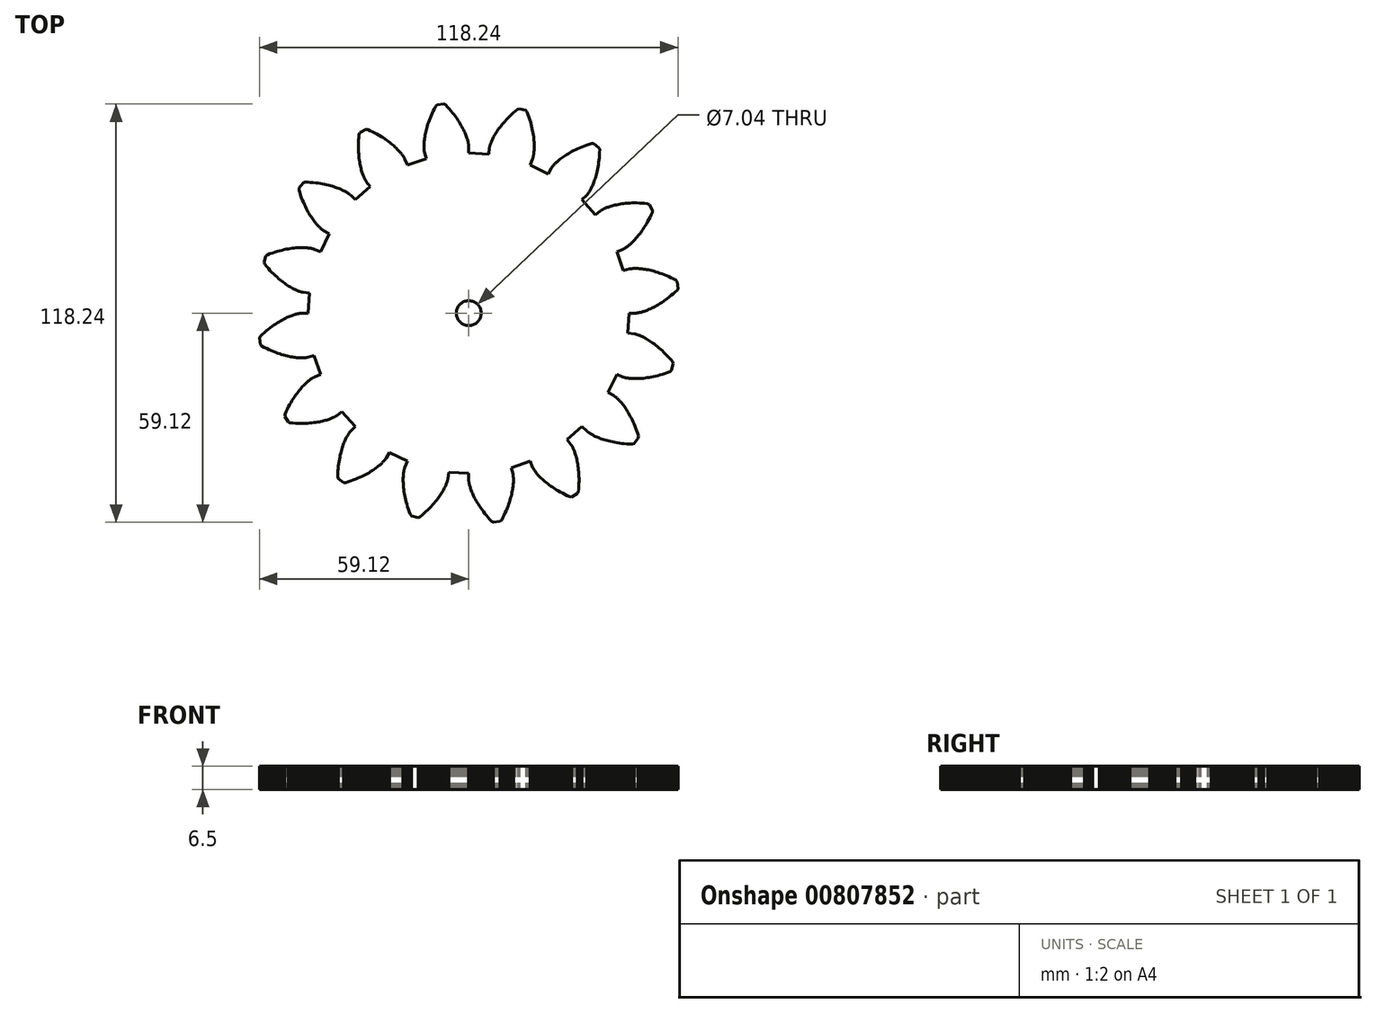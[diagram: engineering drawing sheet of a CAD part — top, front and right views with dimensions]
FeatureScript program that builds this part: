
annotation { "Feature Type Name" : "Feature", "Feature Type Description" : "" }
export const myFeature = defineFeature(function(context is Context, id is Id, definition is map)
    precondition{}
    {
        {
            var Q0;
            Q0=qCreatedBy(makeId("Top.planeOp"),FACE);
            var sketch = newSketch(context, id + "F0", { "sketchPlane" : qUnion([Q0])});
            skLineSegment(sketch, "E0", {"start": v(45.31, 0) * mm, "end": v(47.16, 0) * mm});
            skLineSegment(sketch, "E1", {"start": v(47.16, 0) * mm, "end": v(47.19, 0) * mm});
            skLineSegment(sketch, "E2", {"start": v(47.19, 0) * mm, "end": v(47.24, 0) * mm});
            skLineSegment(sketch, "E3", {"start": v(47.24, 0) * mm, "end": v(47.31, 0) * mm});
            skLineSegment(sketch, "E4", {"start": v(47.31, 0) * mm, "end": v(47.4, 0.02) * mm});
            skLineSegment(sketch, "E5", {"start": v(47.4, 0.02) * mm, "end": v(47.52, 0.03) * mm});
            skLineSegment(sketch, "E6", {"start": v(47.52, 0.03) * mm, "end": v(47.66, 0.05) * mm});
            skLineSegment(sketch, "E7", {"start": v(47.66, 0.05) * mm, "end": v(47.83, 0.08) * mm});
            skLineSegment(sketch, "E8", {"start": v(47.83, 0.08) * mm, "end": v(48, 0.11) * mm});
            skLineSegment(sketch, "E9", {"start": v(48, 0.11) * mm, "end": v(48.21, 0.15) * mm});
            skLineSegment(sketch, "E10", {"start": v(48.21, 0.15) * mm, "end": v(48.44, 0.2) * mm});
            skLineSegment(sketch, "E11", {"start": v(48.44, 0.2) * mm, "end": v(48.69, 0.27) * mm});
            skLineSegment(sketch, "E12", {"start": v(48.69, 0.27) * mm, "end": v(48.95, 0.34) * mm});
            skLineSegment(sketch, "E13", {"start": v(48.95, 0.34) * mm, "end": v(49.24, 0.42) * mm});
            skLineSegment(sketch, "E14", {"start": v(49.24, 0.42) * mm, "end": v(49.54, 0.52) * mm});
            skLineSegment(sketch, "E15", {"start": v(49.54, 0.52) * mm, "end": v(49.87, 0.64) * mm});
            skLineSegment(sketch, "E16", {"start": v(49.87, 0.64) * mm, "end": v(50.21, 0.76) * mm});
            skLineSegment(sketch, "E17", {"start": v(50.21, 0.76) * mm, "end": v(50.57, 0.9) * mm});
            skLineSegment(sketch, "E18", {"start": v(50.57, 0.9) * mm, "end": v(50.95, 1.07) * mm});
            skLineSegment(sketch, "E19", {"start": v(50.95, 1.07) * mm, "end": v(51.34, 1.24) * mm});
            skLineSegment(sketch, "E20", {"start": v(51.34, 1.24) * mm, "end": v(51.76, 1.44) * mm});
            skLineSegment(sketch, "E21", {"start": v(51.76, 1.44) * mm, "end": v(52.18, 1.65) * mm});
            skLineSegment(sketch, "E22", {"start": v(52.18, 1.65) * mm, "end": v(52.63, 1.89) * mm});
            skLineSegment(sketch, "E23", {"start": v(52.63, 1.89) * mm, "end": v(53.08, 2.14) * mm});
            skLineSegment(sketch, "E24", {"start": v(53.08, 2.14) * mm, "end": v(53.55, 2.42) * mm});
            skLineSegment(sketch, "E25", {"start": v(53.55, 2.42) * mm, "end": v(54.04, 2.71) * mm});
            skLineSegment(sketch, "E26", {"start": v(54.04, 2.71) * mm, "end": v(54.53, 3.04) * mm});
            skLineSegment(sketch, "E27", {"start": v(54.53, 3.04) * mm, "end": v(55.04, 3.38) * mm});
            skLineSegment(sketch, "E28", {"start": v(55.04, 3.38) * mm, "end": v(55.56, 3.75) * mm});
            skLineSegment(sketch, "E29", {"start": v(55.56, 3.75) * mm, "end": v(56.08, 4.14) * mm});
            skLineSegment(sketch, "E30", {"start": v(56.08, 4.14) * mm, "end": v(56.62, 4.56) * mm});
            skLineSegment(sketch, "E31", {"start": v(56.62, 4.56) * mm, "end": v(57.17, 5) * mm});
            skLineSegment(sketch, "E32", {"start": v(57.17, 5) * mm, "end": v(57.72, 5.47) * mm});
            skLineSegment(sketch, "E33", {"start": v(57.72, 5.47) * mm, "end": v(58.28, 5.97) * mm});
            skLineSegment(sketch, "E34", {"start": v(58.28, 5.97) * mm, "end": v(58.84, 6.49) * mm});
            skLineSegment(sketch, "E35", {"start": v(58.84, 6.49) * mm, "end": v(59.12, 7) * mm});
            skLineSegment(sketch, "E36", {"start": v(59.12, 7) * mm, "end": v(58.86, 8.9) * mm});
            skLineSegment(sketch, "E37", {"start": v(58.86, 8.9) * mm, "end": v(58.46, 9.33) * mm});
            skLineSegment(sketch, "E38", {"start": v(58.46, 9.33) * mm, "end": v(57.78, 9.68) * mm});
            skLineSegment(sketch, "E39", {"start": v(57.78, 9.68) * mm, "end": v(57.1, 10.01) * mm});
            skLineSegment(sketch, "E40", {"start": v(57.1, 10.01) * mm, "end": v(56.45, 10.32) * mm});
            skLineSegment(sketch, "E41", {"start": v(56.45, 10.32) * mm, "end": v(55.8, 10.6) * mm});
            skLineSegment(sketch, "E42", {"start": v(55.8, 10.6) * mm, "end": v(55.18, 10.86) * mm});
            skLineSegment(sketch, "E43", {"start": v(55.18, 10.86) * mm, "end": v(54.57, 11.1) * mm});
            skLineSegment(sketch, "E44", {"start": v(54.57, 11.1) * mm, "end": v(53.97, 11.32) * mm});
            skLineSegment(sketch, "E45", {"start": v(53.97, 11.32) * mm, "end": v(53.39, 11.52) * mm});
            skLineSegment(sketch, "E46", {"start": v(53.39, 11.52) * mm, "end": v(52.83, 11.7) * mm});
            skLineSegment(sketch, "E47", {"start": v(52.83, 11.7) * mm, "end": v(52.28, 11.85) * mm});
            skLineSegment(sketch, "E48", {"start": v(52.28, 11.85) * mm, "end": v(51.76, 12) * mm});
            skLineSegment(sketch, "E49", {"start": v(51.76, 12) * mm, "end": v(51.25, 12.12) * mm});
            skLineSegment(sketch, "E50", {"start": v(51.25, 12.12) * mm, "end": v(50.76, 12.23) * mm});
            skLineSegment(sketch, "E51", {"start": v(50.76, 12.23) * mm, "end": v(50.3, 12.32) * mm});
            skLineSegment(sketch, "E52", {"start": v(50.3, 12.32) * mm, "end": v(49.84, 12.4) * mm});
            skLineSegment(sketch, "E53", {"start": v(49.84, 12.4) * mm, "end": v(49.41, 12.46) * mm});
            skLineSegment(sketch, "E54", {"start": v(49.41, 12.46) * mm, "end": v(49, 12.52) * mm});
            skLineSegment(sketch, "E55", {"start": v(49, 12.52) * mm, "end": v(48.62, 12.56) * mm});
            skLineSegment(sketch, "E56", {"start": v(48.62, 12.56) * mm, "end": v(48.26, 12.6) * mm});
            skLineSegment(sketch, "E57", {"start": v(48.26, 12.6) * mm, "end": v(47.91, 12.62) * mm});
            skLineSegment(sketch, "E58", {"start": v(47.91, 12.62) * mm, "end": v(47.6, 12.63) * mm});
            skLineSegment(sketch, "E59", {"start": v(47.6, 12.63) * mm, "end": v(47.3, 12.64) * mm});
            skLineSegment(sketch, "E60", {"start": v(47.3, 12.64) * mm, "end": v(47.02, 12.64) * mm});
            skLineSegment(sketch, "E61", {"start": v(47.02, 12.64) * mm, "end": v(46.76, 12.63) * mm});
            skLineSegment(sketch, "E62", {"start": v(46.76, 12.63) * mm, "end": v(46.53, 12.62) * mm});
            skLineSegment(sketch, "E63", {"start": v(46.53, 12.62) * mm, "end": v(46.33, 12.6) * mm});
            skLineSegment(sketch, "E64", {"start": v(46.33, 12.6) * mm, "end": v(46.14, 12.6) * mm});
            skLineSegment(sketch, "E65", {"start": v(46.14, 12.6) * mm, "end": v(45.98, 12.57) * mm});
            skLineSegment(sketch, "E66", {"start": v(45.98, 12.57) * mm, "end": v(45.84, 12.56) * mm});
            skLineSegment(sketch, "E67", {"start": v(45.84, 12.56) * mm, "end": v(45.72, 12.54) * mm});
            skLineSegment(sketch, "E68", {"start": v(45.72, 12.54) * mm, "end": v(45.62, 12.52) * mm});
            skLineSegment(sketch, "E69", {"start": v(45.62, 12.52) * mm, "end": v(45.55, 12.5) * mm});
            skLineSegment(sketch, "E70", {"start": v(45.55, 12.5) * mm, "end": v(45.5, 12.5) * mm});
            skLineSegment(sketch, "E71", {"start": v(45.5, 12.5) * mm, "end": v(45.47, 12.49) * mm});
            skLineSegment(sketch, "E72", {"start": v(45.47, 12.49) * mm, "end": v(43.7, 12) * mm});
            skLineSegment(sketch, "E73", {"start": v(43.7, 12) * mm, "end": v(41.86, 17.34) * mm});
            skLineSegment(sketch, "E74", {"start": v(41.86, 17.34) * mm, "end": v(43.57, 18.05) * mm});
            skLineSegment(sketch, "E75", {"start": v(43.57, 18.05) * mm, "end": v(43.6, 18.06) * mm});
            skLineSegment(sketch, "E76", {"start": v(43.6, 18.06) * mm, "end": v(43.64, 18.08) * mm});
            skLineSegment(sketch, "E77", {"start": v(43.64, 18.08) * mm, "end": v(43.7, 18.11) * mm});
            skLineSegment(sketch, "E78", {"start": v(43.7, 18.11) * mm, "end": v(43.8, 18.16) * mm});
            skLineSegment(sketch, "E79", {"start": v(43.8, 18.16) * mm, "end": v(43.9, 18.22) * mm});
            skLineSegment(sketch, "E80", {"start": v(43.9, 18.22) * mm, "end": v(44.02, 18.29) * mm});
            skLineSegment(sketch, "E81", {"start": v(44.02, 18.29) * mm, "end": v(44.16, 18.37) * mm});
            skLineSegment(sketch, "E82", {"start": v(44.16, 18.37) * mm, "end": v(44.31, 18.48) * mm});
            skLineSegment(sketch, "E83", {"start": v(44.31, 18.48) * mm, "end": v(44.49, 18.6) * mm});
            skLineSegment(sketch, "E84", {"start": v(44.49, 18.6) * mm, "end": v(44.67, 18.73) * mm});
            skLineSegment(sketch, "E85", {"start": v(44.67, 18.73) * mm, "end": v(44.88, 18.88) * mm});
            skLineSegment(sketch, "E86", {"start": v(44.88, 18.88) * mm, "end": v(45.1, 19.05) * mm});
            skLineSegment(sketch, "E87", {"start": v(45.1, 19.05) * mm, "end": v(45.33, 19.23) * mm});
            skLineSegment(sketch, "E88", {"start": v(45.33, 19.23) * mm, "end": v(45.57, 19.44) * mm});
            skLineSegment(sketch, "E89", {"start": v(45.57, 19.44) * mm, "end": v(45.83, 19.67) * mm});
            skLineSegment(sketch, "E90", {"start": v(45.83, 19.67) * mm, "end": v(46.1, 19.92) * mm});
            skLineSegment(sketch, "E91", {"start": v(46.1, 19.92) * mm, "end": v(46.38, 20.2) * mm});
            skLineSegment(sketch, "E92", {"start": v(46.38, 20.2) * mm, "end": v(46.66, 20.48) * mm});
            skLineSegment(sketch, "E93", {"start": v(46.66, 20.48) * mm, "end": v(46.96, 20.8) * mm});
            skLineSegment(sketch, "E94", {"start": v(46.96, 20.8) * mm, "end": v(47.27, 21.13) * mm});
            skLineSegment(sketch, "E95", {"start": v(47.27, 21.13) * mm, "end": v(47.58, 21.5) * mm});
            skLineSegment(sketch, "E96", {"start": v(47.58, 21.5) * mm, "end": v(47.9, 21.88) * mm});
            skLineSegment(sketch, "E97", {"start": v(47.9, 21.88) * mm, "end": v(48.22, 22.3) * mm});
            skLineSegment(sketch, "E98", {"start": v(48.22, 22.3) * mm, "end": v(48.55, 22.73) * mm});
            skLineSegment(sketch, "E99", {"start": v(48.55, 22.73) * mm, "end": v(48.88, 23.19) * mm});
            skLineSegment(sketch, "E100", {"start": v(48.88, 23.19) * mm, "end": v(49.22, 23.67) * mm});
            skLineSegment(sketch, "E101", {"start": v(49.22, 23.67) * mm, "end": v(49.56, 24.18) * mm});
            skLineSegment(sketch, "E102", {"start": v(49.56, 24.18) * mm, "end": v(49.9, 24.72) * mm});
            skLineSegment(sketch, "E103", {"start": v(49.9, 24.72) * mm, "end": v(50.23, 25.29) * mm});
            skLineSegment(sketch, "E104", {"start": v(50.23, 25.29) * mm, "end": v(50.57, 25.88) * mm});
            skLineSegment(sketch, "E105", {"start": v(50.57, 25.88) * mm, "end": v(50.9, 26.5) * mm});
            skLineSegment(sketch, "E106", {"start": v(50.9, 26.5) * mm, "end": v(51.23, 27.14) * mm});
            skLineSegment(sketch, "E107", {"start": v(51.23, 27.14) * mm, "end": v(51.56, 27.81) * mm});
            skLineSegment(sketch, "E108", {"start": v(51.56, 27.81) * mm, "end": v(51.88, 28.51) * mm});
            skLineSegment(sketch, "E109", {"start": v(51.88, 28.51) * mm, "end": v(51.94, 29.1) * mm});
            skLineSegment(sketch, "E110", {"start": v(51.94, 29.1) * mm, "end": v(50.98, 30.75) * mm});
            skLineSegment(sketch, "E111", {"start": v(50.98, 30.75) * mm, "end": v(50.44, 30.99) * mm});
            skLineSegment(sketch, "E112", {"start": v(50.44, 30.99) * mm, "end": v(49.67, 31.05) * mm});
            skLineSegment(sketch, "E113", {"start": v(49.67, 31.05) * mm, "end": v(48.93, 31.1) * mm});
            skLineSegment(sketch, "E114", {"start": v(48.93, 31.1) * mm, "end": v(48.2, 31.14) * mm});
            skLineSegment(sketch, "E115", {"start": v(48.2, 31.14) * mm, "end": v(47.5, 31.15) * mm});
            skLineSegment(sketch, "E116", {"start": v(47.5, 31.15) * mm, "end": v(46.82, 31.15) * mm});
            skLineSegment(sketch, "E117", {"start": v(46.82, 31.15) * mm, "end": v(46.16, 31.14) * mm});
            skLineSegment(sketch, "E118", {"start": v(46.16, 31.14) * mm, "end": v(45.53, 31.1) * mm});
            skLineSegment(sketch, "E119", {"start": v(45.53, 31.1) * mm, "end": v(44.92, 31.07) * mm});
            skLineSegment(sketch, "E120", {"start": v(44.92, 31.07) * mm, "end": v(44.33, 31.02) * mm});
            skLineSegment(sketch, "E121", {"start": v(44.33, 31.02) * mm, "end": v(43.77, 30.96) * mm});
            skLineSegment(sketch, "E122", {"start": v(43.77, 30.96) * mm, "end": v(43.23, 30.89) * mm});
            skLineSegment(sketch, "E123", {"start": v(43.23, 30.89) * mm, "end": v(42.7, 30.8) * mm});
            skLineSegment(sketch, "E124", {"start": v(42.7, 30.8) * mm, "end": v(42.22, 30.72) * mm});
            skLineSegment(sketch, "E125", {"start": v(42.22, 30.72) * mm, "end": v(41.75, 30.63) * mm});
            skLineSegment(sketch, "E126", {"start": v(41.75, 30.63) * mm, "end": v(41.3, 30.53) * mm});
            skLineSegment(sketch, "E127", {"start": v(41.3, 30.53) * mm, "end": v(40.88, 30.43) * mm});
            skLineSegment(sketch, "E128", {"start": v(40.88, 30.43) * mm, "end": v(40.49, 30.32) * mm});
            skLineSegment(sketch, "E129", {"start": v(40.49, 30.32) * mm, "end": v(40.11, 30.21) * mm});
            skLineSegment(sketch, "E130", {"start": v(40.11, 30.21) * mm, "end": v(39.76, 30.1) * mm});
            skLineSegment(sketch, "E131", {"start": v(39.76, 30.1) * mm, "end": v(39.44, 30) * mm});
            skLineSegment(sketch, "E132", {"start": v(39.44, 30) * mm, "end": v(39.14, 29.88) * mm});
            skLineSegment(sketch, "E133", {"start": v(39.14, 29.88) * mm, "end": v(38.86, 29.77) * mm});
            skLineSegment(sketch, "E134", {"start": v(38.86, 29.77) * mm, "end": v(38.6, 29.67) * mm});
            skLineSegment(sketch, "E135", {"start": v(38.6, 29.67) * mm, "end": v(38.37, 29.57) * mm});
            skLineSegment(sketch, "E136", {"start": v(38.37, 29.57) * mm, "end": v(38.16, 29.47) * mm});
            skLineSegment(sketch, "E137", {"start": v(38.16, 29.47) * mm, "end": v(37.97, 29.38) * mm});
            skLineSegment(sketch, "E138", {"start": v(37.97, 29.38) * mm, "end": v(37.8, 29.3) * mm});
            skLineSegment(sketch, "E139", {"start": v(37.8, 29.3) * mm, "end": v(37.67, 29.21) * mm});
            skLineSegment(sketch, "E140", {"start": v(37.67, 29.21) * mm, "end": v(37.54, 29.14) * mm});
            skLineSegment(sketch, "E141", {"start": v(37.54, 29.14) * mm, "end": v(37.44, 29.08) * mm});
            skLineSegment(sketch, "E142", {"start": v(37.44, 29.08) * mm, "end": v(37.36, 29.03) * mm});
            skLineSegment(sketch, "E143", {"start": v(37.36, 29.03) * mm, "end": v(37.3, 28.99) * mm});
            skLineSegment(sketch, "E144", {"start": v(37.3, 28.99) * mm, "end": v(37.26, 28.96) * mm});
            skLineSegment(sketch, "E145", {"start": v(37.26, 28.96) * mm, "end": v(37.23, 28.94) * mm});
            skLineSegment(sketch, "E146", {"start": v(37.23, 28.94) * mm, "end": v(35.77, 27.8) * mm});
            skLineSegment(sketch, "E147", {"start": v(35.77, 27.8) * mm, "end": v(32.04, 32.04) * mm});
            skLineSegment(sketch, "E148", {"start": v(32.04, 32.04) * mm, "end": v(33.34, 33.34) * mm});
            skLineSegment(sketch, "E149", {"start": v(33.34, 33.34) * mm, "end": v(33.36, 33.37) * mm});
            skLineSegment(sketch, "E150", {"start": v(33.36, 33.37) * mm, "end": v(33.4, 33.4) * mm});
            skLineSegment(sketch, "E151", {"start": v(33.4, 33.4) * mm, "end": v(33.45, 33.46) * mm});
            skLineSegment(sketch, "E152", {"start": v(33.45, 33.46) * mm, "end": v(33.5, 33.53) * mm});
            skLineSegment(sketch, "E153", {"start": v(33.5, 33.53) * mm, "end": v(33.58, 33.63) * mm});
            skLineSegment(sketch, "E154", {"start": v(33.58, 33.63) * mm, "end": v(33.67, 33.74) * mm});
            skLineSegment(sketch, "E155", {"start": v(33.67, 33.74) * mm, "end": v(33.76, 33.87) * mm});
            skLineSegment(sketch, "E156", {"start": v(33.76, 33.87) * mm, "end": v(33.87, 34.03) * mm});
            skLineSegment(sketch, "E157", {"start": v(33.87, 34.03) * mm, "end": v(33.99, 34.2) * mm});
            skLineSegment(sketch, "E158", {"start": v(33.99, 34.2) * mm, "end": v(34.1, 34.4) * mm});
            skLineSegment(sketch, "E159", {"start": v(34.1, 34.4) * mm, "end": v(34.24, 34.61) * mm});
            skLineSegment(sketch, "E160", {"start": v(34.24, 34.61) * mm, "end": v(34.37, 34.85) * mm});
            skLineSegment(sketch, "E161", {"start": v(34.37, 34.85) * mm, "end": v(34.52, 35.12) * mm});
            skLineSegment(sketch, "E162", {"start": v(34.52, 35.12) * mm, "end": v(34.66, 35.4) * mm});
            skLineSegment(sketch, "E163", {"start": v(34.66, 35.4) * mm, "end": v(34.81, 35.71) * mm});
            skLineSegment(sketch, "E164", {"start": v(34.81, 35.71) * mm, "end": v(34.96, 36.04) * mm});
            skLineSegment(sketch, "E165", {"start": v(34.96, 36.04) * mm, "end": v(35.12, 36.4) * mm});
            skLineSegment(sketch, "E166", {"start": v(35.12, 36.4) * mm, "end": v(35.27, 36.78) * mm});
            skLineSegment(sketch, "E167", {"start": v(35.27, 36.78) * mm, "end": v(35.43, 37.18) * mm});
            skLineSegment(sketch, "E168", {"start": v(35.43, 37.18) * mm, "end": v(35.58, 37.61) * mm});
            skLineSegment(sketch, "E169", {"start": v(35.58, 37.61) * mm, "end": v(35.73, 38.07) * mm});
            skLineSegment(sketch, "E170", {"start": v(35.73, 38.07) * mm, "end": v(35.88, 38.55) * mm});
            skLineSegment(sketch, "E171", {"start": v(35.88, 38.55) * mm, "end": v(36.02, 39.05) * mm});
            skLineSegment(sketch, "E172", {"start": v(36.02, 39.05) * mm, "end": v(36.16, 39.58) * mm});
            skLineSegment(sketch, "E173", {"start": v(36.16, 39.58) * mm, "end": v(36.3, 40.13) * mm});
            skLineSegment(sketch, "E174", {"start": v(36.3, 40.13) * mm, "end": v(36.41, 40.7) * mm});
            skLineSegment(sketch, "E175", {"start": v(36.41, 40.7) * mm, "end": v(36.53, 41.3) * mm});
            skLineSegment(sketch, "E176", {"start": v(36.53, 41.3) * mm, "end": v(36.64, 41.93) * mm});
            skLineSegment(sketch, "E177", {"start": v(36.64, 41.93) * mm, "end": v(36.73, 42.58) * mm});
            skLineSegment(sketch, "E178", {"start": v(36.73, 42.58) * mm, "end": v(36.82, 43.26) * mm});
            skLineSegment(sketch, "E179", {"start": v(36.82, 43.26) * mm, "end": v(36.89, 43.96) * mm});
            skLineSegment(sketch, "E180", {"start": v(36.89, 43.96) * mm, "end": v(36.95, 44.68) * mm});
            skLineSegment(sketch, "E181", {"start": v(36.95, 44.68) * mm, "end": v(36.99, 45.43) * mm});
            skLineSegment(sketch, "E182", {"start": v(36.99, 45.43) * mm, "end": v(37.02, 46.2) * mm});
            skLineSegment(sketch, "E183", {"start": v(37.02, 46.2) * mm, "end": v(36.85, 46.76) * mm});
            skLineSegment(sketch, "E184", {"start": v(36.85, 46.76) * mm, "end": v(35.33, 47.91) * mm});
            skLineSegment(sketch, "E185", {"start": v(35.33, 47.91) * mm, "end": v(34.74, 47.93) * mm});
            skLineSegment(sketch, "E186", {"start": v(34.74, 47.93) * mm, "end": v(34, 47.7) * mm});
            skLineSegment(sketch, "E187", {"start": v(34, 47.7) * mm, "end": v(33.3, 47.46) * mm});
            skLineSegment(sketch, "E188", {"start": v(33.3, 47.46) * mm, "end": v(32.62, 47.21) * mm});
            skLineSegment(sketch, "E189", {"start": v(32.62, 47.21) * mm, "end": v(31.96, 46.96) * mm});
            skLineSegment(sketch, "E190", {"start": v(31.96, 46.96) * mm, "end": v(31.34, 46.7) * mm});
            skLineSegment(sketch, "E191", {"start": v(31.34, 46.7) * mm, "end": v(30.73, 46.43) * mm});
            skLineSegment(sketch, "E192", {"start": v(30.73, 46.43) * mm, "end": v(30.16, 46.16) * mm});
            skLineSegment(sketch, "E193", {"start": v(30.16, 46.16) * mm, "end": v(29.61, 45.9) * mm});
            skLineSegment(sketch, "E194", {"start": v(29.61, 45.9) * mm, "end": v(29.09, 45.62) * mm});
            skLineSegment(sketch, "E195", {"start": v(29.09, 45.62) * mm, "end": v(28.59, 45.35) * mm});
            skLineSegment(sketch, "E196", {"start": v(28.59, 45.35) * mm, "end": v(28.12, 45.08) * mm});
            skLineSegment(sketch, "E197", {"start": v(28.12, 45.08) * mm, "end": v(27.67, 44.8) * mm});
            skLineSegment(sketch, "E198", {"start": v(27.67, 44.8) * mm, "end": v(27.25, 44.54) * mm});
            skLineSegment(sketch, "E199", {"start": v(27.25, 44.54) * mm, "end": v(26.85, 44.27) * mm});
            skLineSegment(sketch, "E200", {"start": v(26.85, 44.27) * mm, "end": v(26.48, 44.01) * mm});
            skLineSegment(sketch, "E201", {"start": v(26.48, 44.01) * mm, "end": v(26.13, 43.75) * mm});
            skLineSegment(sketch, "E202", {"start": v(26.13, 43.75) * mm, "end": v(25.8, 43.5) * mm});
            skLineSegment(sketch, "E203", {"start": v(25.8, 43.5) * mm, "end": v(25.5, 43.26) * mm});
            skLineSegment(sketch, "E204", {"start": v(25.5, 43.26) * mm, "end": v(25.22, 43.03) * mm});
            skLineSegment(sketch, "E205", {"start": v(25.22, 43.03) * mm, "end": v(24.96, 42.8) * mm});
            skLineSegment(sketch, "E206", {"start": v(24.96, 42.8) * mm, "end": v(24.72, 42.58) * mm});
            skLineSegment(sketch, "E207", {"start": v(24.72, 42.58) * mm, "end": v(24.5, 42.38) * mm});
            skLineSegment(sketch, "E208", {"start": v(24.5, 42.38) * mm, "end": v(24.31, 42.18) * mm});
            skLineSegment(sketch, "E209", {"start": v(24.31, 42.18) * mm, "end": v(24.14, 42) * mm});
            skLineSegment(sketch, "E210", {"start": v(24.14, 42) * mm, "end": v(23.98, 41.83) * mm});
            skLineSegment(sketch, "E211", {"start": v(23.98, 41.83) * mm, "end": v(23.84, 41.67) * mm});
            skLineSegment(sketch, "E212", {"start": v(23.84, 41.67) * mm, "end": v(23.72, 41.53) * mm});
            skLineSegment(sketch, "E213", {"start": v(23.72, 41.53) * mm, "end": v(23.62, 41.4) * mm});
            skLineSegment(sketch, "E214", {"start": v(23.62, 41.4) * mm, "end": v(23.53, 41.29) * mm});
            skLineSegment(sketch, "E215", {"start": v(23.53, 41.29) * mm, "end": v(23.46, 41.2) * mm});
            skLineSegment(sketch, "E216", {"start": v(23.46, 41.2) * mm, "end": v(23.4, 41.12) * mm});
            skLineSegment(sketch, "E217", {"start": v(23.4, 41.12) * mm, "end": v(23.37, 41.05) * mm});
            skLineSegment(sketch, "E218", {"start": v(23.37, 41.05) * mm, "end": v(23.34, 41) * mm});
            skLineSegment(sketch, "E219", {"start": v(23.34, 41) * mm, "end": v(23.32, 40.98) * mm});
            skLineSegment(sketch, "E220", {"start": v(23.32, 40.98) * mm, "end": v(22.4, 39.38) * mm});
            skLineSegment(sketch, "E221", {"start": v(22.4, 39.38) * mm, "end": v(17.34, 41.86) * mm});
            skLineSegment(sketch, "E222", {"start": v(17.34, 41.86) * mm, "end": v(18.05, 43.57) * mm});
            skLineSegment(sketch, "E223", {"start": v(18.05, 43.57) * mm, "end": v(18.06, 43.6) * mm});
            skLineSegment(sketch, "E224", {"start": v(18.06, 43.6) * mm, "end": v(18.07, 43.64) * mm});
            skLineSegment(sketch, "E225", {"start": v(18.07, 43.64) * mm, "end": v(18.1, 43.71) * mm});
            skLineSegment(sketch, "E226", {"start": v(18.1, 43.71) * mm, "end": v(18.13, 43.8) * mm});
            skLineSegment(sketch, "E227", {"start": v(18.13, 43.8) * mm, "end": v(18.16, 43.92) * mm});
            skLineSegment(sketch, "E228", {"start": v(18.16, 43.92) * mm, "end": v(18.2, 44.06) * mm});
            skLineSegment(sketch, "E229", {"start": v(18.2, 44.06) * mm, "end": v(18.23, 44.22) * mm});
            skLineSegment(sketch, "E230", {"start": v(18.23, 44.22) * mm, "end": v(18.27, 44.4) * mm});
            skLineSegment(sketch, "E231", {"start": v(18.27, 44.4) * mm, "end": v(18.3, 44.6) * mm});
            skLineSegment(sketch, "E232", {"start": v(18.3, 44.6) * mm, "end": v(18.35, 44.83) * mm});
            skLineSegment(sketch, "E233", {"start": v(18.35, 44.83) * mm, "end": v(18.39, 45.08) * mm});
            skLineSegment(sketch, "E234", {"start": v(18.39, 45.08) * mm, "end": v(18.42, 45.36) * mm});
            skLineSegment(sketch, "E235", {"start": v(18.42, 45.36) * mm, "end": v(18.45, 45.65) * mm});
            skLineSegment(sketch, "E236", {"start": v(18.45, 45.65) * mm, "end": v(18.48, 45.97) * mm});
            skLineSegment(sketch, "E237", {"start": v(18.48, 45.97) * mm, "end": v(18.5, 46.31) * mm});
            skLineSegment(sketch, "E238", {"start": v(18.5, 46.31) * mm, "end": v(18.51, 46.68) * mm});
            skLineSegment(sketch, "E239", {"start": v(18.51, 46.68) * mm, "end": v(18.52, 47.07) * mm});
            skLineSegment(sketch, "E240", {"start": v(18.52, 47.07) * mm, "end": v(18.51, 47.48) * mm});
            skLineSegment(sketch, "E241", {"start": v(18.51, 47.48) * mm, "end": v(18.5, 47.91) * mm});
            skLineSegment(sketch, "E242", {"start": v(18.5, 47.91) * mm, "end": v(18.48, 48.37) * mm});
            skLineSegment(sketch, "E243", {"start": v(18.48, 48.37) * mm, "end": v(18.44, 48.84) * mm});
            skLineSegment(sketch, "E244", {"start": v(18.44, 48.84) * mm, "end": v(18.4, 49.34) * mm});
            skLineSegment(sketch, "E245", {"start": v(18.4, 49.34) * mm, "end": v(18.34, 49.86) * mm});
            skLineSegment(sketch, "E246", {"start": v(18.34, 49.86) * mm, "end": v(18.26, 50.4) * mm});
            skLineSegment(sketch, "E247", {"start": v(18.26, 50.4) * mm, "end": v(18.17, 50.96) * mm});
            skLineSegment(sketch, "E248", {"start": v(18.17, 50.96) * mm, "end": v(18.06, 51.54) * mm});
            skLineSegment(sketch, "E249", {"start": v(18.06, 51.54) * mm, "end": v(17.94, 52.14) * mm});
            skLineSegment(sketch, "E250", {"start": v(17.94, 52.14) * mm, "end": v(17.8, 52.76) * mm});
            skLineSegment(sketch, "E251", {"start": v(17.8, 52.76) * mm, "end": v(17.64, 53.4) * mm});
            skLineSegment(sketch, "E252", {"start": v(17.64, 53.4) * mm, "end": v(17.46, 54.06) * mm});
            skLineSegment(sketch, "E253", {"start": v(17.46, 54.06) * mm, "end": v(17.26, 54.73) * mm});
            skLineSegment(sketch, "E254", {"start": v(17.26, 54.73) * mm, "end": v(17.04, 55.42) * mm});
            skLineSegment(sketch, "E255", {"start": v(17.04, 55.42) * mm, "end": v(16.8, 56.12) * mm});
            skLineSegment(sketch, "E256", {"start": v(16.8, 56.12) * mm, "end": v(16.52, 56.85) * mm});
            skLineSegment(sketch, "E257", {"start": v(16.52, 56.85) * mm, "end": v(16.15, 57.3) * mm});
            skLineSegment(sketch, "E258", {"start": v(16.15, 57.3) * mm, "end": v(14.3, 57.79) * mm});
            skLineSegment(sketch, "E259", {"start": v(14.3, 57.79) * mm, "end": v(13.76, 57.58) * mm});
            skLineSegment(sketch, "E260", {"start": v(13.76, 57.58) * mm, "end": v(13.17, 57.08) * mm});
            skLineSegment(sketch, "E261", {"start": v(13.17, 57.08) * mm, "end": v(12.6, 56.6) * mm});
            skLineSegment(sketch, "E262", {"start": v(12.6, 56.6) * mm, "end": v(12.07, 56.1) * mm});
            skLineSegment(sketch, "E263", {"start": v(12.07, 56.1) * mm, "end": v(11.56, 55.62) * mm});
            skLineSegment(sketch, "E264", {"start": v(11.56, 55.62) * mm, "end": v(11.08, 55.14) * mm});
            skLineSegment(sketch, "E265", {"start": v(11.08, 55.14) * mm, "end": v(10.63, 54.66) * mm});
            skLineSegment(sketch, "E266", {"start": v(10.63, 54.66) * mm, "end": v(10.2, 54.2) * mm});
            skLineSegment(sketch, "E267", {"start": v(10.2, 54.2) * mm, "end": v(9.8, 53.73) * mm});
            skLineSegment(sketch, "E268", {"start": v(9.8, 53.73) * mm, "end": v(9.41, 53.28) * mm});
            skLineSegment(sketch, "E269", {"start": v(9.41, 53.28) * mm, "end": v(9.06, 52.84) * mm});
            skLineSegment(sketch, "E270", {"start": v(9.06, 52.84) * mm, "end": v(8.73, 52.4) * mm});
            skLineSegment(sketch, "E271", {"start": v(8.73, 52.4) * mm, "end": v(8.42, 51.98) * mm});
            skLineSegment(sketch, "E272", {"start": v(8.42, 51.98) * mm, "end": v(8.13, 51.57) * mm});
            skLineSegment(sketch, "E273", {"start": v(8.13, 51.57) * mm, "end": v(7.86, 51.18) * mm});
            skLineSegment(sketch, "E274", {"start": v(7.86, 51.18) * mm, "end": v(7.62, 50.8) * mm});
            skLineSegment(sketch, "E275", {"start": v(7.62, 50.8) * mm, "end": v(7.4, 50.42) * mm});
            skLineSegment(sketch, "E276", {"start": v(7.4, 50.42) * mm, "end": v(7.19, 50.07) * mm});
            skLineSegment(sketch, "E277", {"start": v(7.19, 50.07) * mm, "end": v(7, 49.73) * mm});
            skLineSegment(sketch, "E278", {"start": v(7, 49.73) * mm, "end": v(6.83, 49.4) * mm});
            skLineSegment(sketch, "E279", {"start": v(6.83, 49.4) * mm, "end": v(6.68, 49.1) * mm});
            skLineSegment(sketch, "E280", {"start": v(6.68, 49.1) * mm, "end": v(6.54, 48.8) * mm});
            skLineSegment(sketch, "E281", {"start": v(6.54, 48.8) * mm, "end": v(6.42, 48.53) * mm});
            skLineSegment(sketch, "E282", {"start": v(6.42, 48.53) * mm, "end": v(6.32, 48.27) * mm});
            skLineSegment(sketch, "E283", {"start": v(6.32, 48.27) * mm, "end": v(6.23, 48.04) * mm});
            skLineSegment(sketch, "E284", {"start": v(6.23, 48.04) * mm, "end": v(6.15, 47.82) * mm});
            skLineSegment(sketch, "E285", {"start": v(6.15, 47.82) * mm, "end": v(6.08, 47.62) * mm});
            skLineSegment(sketch, "E286", {"start": v(6.08, 47.62) * mm, "end": v(6.02, 47.45) * mm});
            skLineSegment(sketch, "E287", {"start": v(6.02, 47.45) * mm, "end": v(5.98, 47.29) * mm});
            skLineSegment(sketch, "E288", {"start": v(5.98, 47.29) * mm, "end": v(5.94, 47.15) * mm});
            skLineSegment(sketch, "E289", {"start": v(5.94, 47.15) * mm, "end": v(5.91, 47.04) * mm});
            skLineSegment(sketch, "E290", {"start": v(5.91, 47.04) * mm, "end": v(5.9, 46.94) * mm});
            skLineSegment(sketch, "E291", {"start": v(5.9, 46.94) * mm, "end": v(5.88, 46.87) * mm});
            skLineSegment(sketch, "E292", {"start": v(5.88, 46.87) * mm, "end": v(5.87, 46.82) * mm});
            skLineSegment(sketch, "E293", {"start": v(5.87, 46.82) * mm, "end": v(5.86, 46.79) * mm});
            skLineSegment(sketch, "E294", {"start": v(5.86, 46.79) * mm, "end": v(5.64, 44.96) * mm});
            skLineSegment(sketch, "E295", {"start": v(5.64, 44.96) * mm, "end": v(0, 45.31) * mm});
            skLineSegment(sketch, "E296", {"start": v(0, 45.31) * mm, "end": v(0, 47.16) * mm});
            skLineSegment(sketch, "E297", {"start": v(0, 47.16) * mm, "end": v(0, 47.19) * mm});
            skLineSegment(sketch, "E298", {"start": v(0, 47.19) * mm, "end": v(0, 47.24) * mm});
            skLineSegment(sketch, "E299", {"start": v(0, 47.24) * mm, "end": v(0, 47.31) * mm});
            skLineSegment(sketch, "E300", {"start": v(0, 47.31) * mm, "end": v(-0.02, 47.4) * mm});
            skLineSegment(sketch, "E301", {"start": v(-0.02, 47.4) * mm, "end": v(-0.03, 47.52) * mm});
            skLineSegment(sketch, "E302", {"start": v(-0.03, 47.52) * mm, "end": v(-0.05, 47.66) * mm});
            skLineSegment(sketch, "E303", {"start": v(-0.05, 47.66) * mm, "end": v(-0.08, 47.83) * mm});
            skLineSegment(sketch, "E304", {"start": v(-0.08, 47.83) * mm, "end": v(-0.1, 48) * mm});
            skLineSegment(sketch, "E305", {"start": v(-0.1, 48) * mm, "end": v(-0.15, 48.21) * mm});
            skLineSegment(sketch, "E306", {"start": v(-0.15, 48.21) * mm, "end": v(-0.2, 48.44) * mm});
            skLineSegment(sketch, "E307", {"start": v(-0.2, 48.44) * mm, "end": v(-0.27, 48.69) * mm});
            skLineSegment(sketch, "E308", {"start": v(-0.27, 48.69) * mm, "end": v(-0.34, 48.95) * mm});
            skLineSegment(sketch, "E309", {"start": v(-0.34, 48.95) * mm, "end": v(-0.42, 49.24) * mm});
            skLineSegment(sketch, "E310", {"start": v(-0.42, 49.24) * mm, "end": v(-0.52, 49.54) * mm});
            skLineSegment(sketch, "E311", {"start": v(-0.52, 49.54) * mm, "end": v(-0.64, 49.87) * mm});
            skLineSegment(sketch, "E312", {"start": v(-0.64, 49.87) * mm, "end": v(-0.76, 50.21) * mm});
            skLineSegment(sketch, "E313", {"start": v(-0.76, 50.21) * mm, "end": v(-0.9, 50.57) * mm});
            skLineSegment(sketch, "E314", {"start": v(-0.9, 50.57) * mm, "end": v(-1.07, 50.95) * mm});
            skLineSegment(sketch, "E315", {"start": v(-1.07, 50.95) * mm, "end": v(-1.24, 51.34) * mm});
            skLineSegment(sketch, "E316", {"start": v(-1.24, 51.34) * mm, "end": v(-1.44, 51.76) * mm});
            skLineSegment(sketch, "E317", {"start": v(-1.44, 51.76) * mm, "end": v(-1.65, 52.18) * mm});
            skLineSegment(sketch, "E318", {"start": v(-1.65, 52.18) * mm, "end": v(-1.89, 52.63) * mm});
            skLineSegment(sketch, "E319", {"start": v(-1.89, 52.63) * mm, "end": v(-2.14, 53.08) * mm});
            skLineSegment(sketch, "E320", {"start": v(-2.14, 53.08) * mm, "end": v(-2.42, 53.55) * mm});
            skLineSegment(sketch, "E321", {"start": v(-2.42, 53.55) * mm, "end": v(-2.71, 54.04) * mm});
            skLineSegment(sketch, "E322", {"start": v(-2.71, 54.04) * mm, "end": v(-3.04, 54.53) * mm});
            skLineSegment(sketch, "E323", {"start": v(-3.04, 54.53) * mm, "end": v(-3.38, 55.04) * mm});
            skLineSegment(sketch, "E324", {"start": v(-3.38, 55.04) * mm, "end": v(-3.75, 55.56) * mm});
            skLineSegment(sketch, "E325", {"start": v(-3.75, 55.56) * mm, "end": v(-4.14, 56.08) * mm});
            skLineSegment(sketch, "E326", {"start": v(-4.14, 56.08) * mm, "end": v(-4.56, 56.62) * mm});
            skLineSegment(sketch, "E327", {"start": v(-4.56, 56.62) * mm, "end": v(-5, 57.17) * mm});
            skLineSegment(sketch, "E328", {"start": v(-5, 57.17) * mm, "end": v(-5.47, 57.72) * mm});
            skLineSegment(sketch, "E329", {"start": v(-5.47, 57.72) * mm, "end": v(-5.97, 58.28) * mm});
            skLineSegment(sketch, "E330", {"start": v(-5.97, 58.28) * mm, "end": v(-6.49, 58.84) * mm});
            skLineSegment(sketch, "E331", {"start": v(-6.49, 58.84) * mm, "end": v(-7, 59.12) * mm});
            skLineSegment(sketch, "E332", {"start": v(-7, 59.12) * mm, "end": v(-8.9, 58.86) * mm});
            skLineSegment(sketch, "E333", {"start": v(-8.9, 58.86) * mm, "end": v(-9.33, 58.46) * mm});
            skLineSegment(sketch, "E334", {"start": v(-9.33, 58.46) * mm, "end": v(-9.68, 57.78) * mm});
            skLineSegment(sketch, "E335", {"start": v(-9.68, 57.78) * mm, "end": v(-10.01, 57.1) * mm});
            skLineSegment(sketch, "E336", {"start": v(-10.01, 57.1) * mm, "end": v(-10.32, 56.45) * mm});
            skLineSegment(sketch, "E337", {"start": v(-10.32, 56.45) * mm, "end": v(-10.6, 55.8) * mm});
            skLineSegment(sketch, "E338", {"start": v(-10.6, 55.8) * mm, "end": v(-10.86, 55.18) * mm});
            skLineSegment(sketch, "E339", {"start": v(-10.86, 55.18) * mm, "end": v(-11.1, 54.57) * mm});
            skLineSegment(sketch, "E340", {"start": v(-11.1, 54.57) * mm, "end": v(-11.32, 53.97) * mm});
            skLineSegment(sketch, "E341", {"start": v(-11.32, 53.97) * mm, "end": v(-11.52, 53.39) * mm});
            skLineSegment(sketch, "E342", {"start": v(-11.52, 53.39) * mm, "end": v(-11.7, 52.83) * mm});
            skLineSegment(sketch, "E343", {"start": v(-11.7, 52.83) * mm, "end": v(-11.85, 52.28) * mm});
            skLineSegment(sketch, "E344", {"start": v(-11.85, 52.28) * mm, "end": v(-12, 51.76) * mm});
            skLineSegment(sketch, "E345", {"start": v(-12, 51.76) * mm, "end": v(-12.12, 51.25) * mm});
            skLineSegment(sketch, "E346", {"start": v(-12.12, 51.25) * mm, "end": v(-12.23, 50.76) * mm});
            skLineSegment(sketch, "E347", {"start": v(-12.23, 50.76) * mm, "end": v(-12.32, 50.3) * mm});
            skLineSegment(sketch, "E348", {"start": v(-12.32, 50.3) * mm, "end": v(-12.4, 49.84) * mm});
            skLineSegment(sketch, "E349", {"start": v(-12.4, 49.84) * mm, "end": v(-12.46, 49.41) * mm});
            skLineSegment(sketch, "E350", {"start": v(-12.46, 49.41) * mm, "end": v(-12.52, 49) * mm});
            skLineSegment(sketch, "E351", {"start": v(-12.52, 49) * mm, "end": v(-12.56, 48.62) * mm});
            skLineSegment(sketch, "E352", {"start": v(-12.56, 48.62) * mm, "end": v(-12.6, 48.26) * mm});
            skLineSegment(sketch, "E353", {"start": v(-12.6, 48.26) * mm, "end": v(-12.62, 47.91) * mm});
            skLineSegment(sketch, "E354", {"start": v(-12.62, 47.91) * mm, "end": v(-12.63, 47.6) * mm});
            skLineSegment(sketch, "E355", {"start": v(-12.63, 47.6) * mm, "end": v(-12.64, 47.3) * mm});
            skLineSegment(sketch, "E356", {"start": v(-12.64, 47.3) * mm, "end": v(-12.64, 47.02) * mm});
            skLineSegment(sketch, "E357", {"start": v(-12.64, 47.02) * mm, "end": v(-12.63, 46.76) * mm});
            skLineSegment(sketch, "E358", {"start": v(-12.63, 46.76) * mm, "end": v(-12.62, 46.53) * mm});
            skLineSegment(sketch, "E359", {"start": v(-12.62, 46.53) * mm, "end": v(-12.6, 46.33) * mm});
            skLineSegment(sketch, "E360", {"start": v(-12.6, 46.33) * mm, "end": v(-12.6, 46.14) * mm});
            skLineSegment(sketch, "E361", {"start": v(-12.6, 46.14) * mm, "end": v(-12.57, 45.98) * mm});
            skLineSegment(sketch, "E362", {"start": v(-12.57, 45.98) * mm, "end": v(-12.56, 45.84) * mm});
            skLineSegment(sketch, "E363", {"start": v(-12.56, 45.84) * mm, "end": v(-12.54, 45.72) * mm});
            skLineSegment(sketch, "E364", {"start": v(-12.54, 45.72) * mm, "end": v(-12.52, 45.62) * mm});
            skLineSegment(sketch, "E365", {"start": v(-12.52, 45.62) * mm, "end": v(-12.5, 45.55) * mm});
            skLineSegment(sketch, "E366", {"start": v(-12.5, 45.55) * mm, "end": v(-12.5, 45.5) * mm});
            skLineSegment(sketch, "E367", {"start": v(-12.5, 45.5) * mm, "end": v(-12.49, 45.47) * mm});
            skLineSegment(sketch, "E368", {"start": v(-12.49, 45.47) * mm, "end": v(-12, 43.7) * mm});
            skLineSegment(sketch, "E369", {"start": v(-12, 43.7) * mm, "end": v(-17.34, 41.86) * mm});
            skLineSegment(sketch, "E370", {"start": v(-17.34, 41.86) * mm, "end": v(-18.05, 43.57) * mm});
            skLineSegment(sketch, "E371", {"start": v(-18.05, 43.57) * mm, "end": v(-18.06, 43.6) * mm});
            skLineSegment(sketch, "E372", {"start": v(-18.06, 43.6) * mm, "end": v(-18.08, 43.64) * mm});
            skLineSegment(sketch, "E373", {"start": v(-18.08, 43.64) * mm, "end": v(-18.11, 43.7) * mm});
            skLineSegment(sketch, "E374", {"start": v(-18.11, 43.7) * mm, "end": v(-18.16, 43.8) * mm});
            skLineSegment(sketch, "E375", {"start": v(-18.16, 43.8) * mm, "end": v(-18.22, 43.9) * mm});
            skLineSegment(sketch, "E376", {"start": v(-18.22, 43.9) * mm, "end": v(-18.29, 44.02) * mm});
            skLineSegment(sketch, "E377", {"start": v(-18.29, 44.02) * mm, "end": v(-18.37, 44.16) * mm});
            skLineSegment(sketch, "E378", {"start": v(-18.37, 44.16) * mm, "end": v(-18.48, 44.31) * mm});
            skLineSegment(sketch, "E379", {"start": v(-18.48, 44.31) * mm, "end": v(-18.6, 44.49) * mm});
            skLineSegment(sketch, "E380", {"start": v(-18.6, 44.49) * mm, "end": v(-18.73, 44.67) * mm});
            skLineSegment(sketch, "E381", {"start": v(-18.73, 44.67) * mm, "end": v(-18.88, 44.88) * mm});
            skLineSegment(sketch, "E382", {"start": v(-18.88, 44.88) * mm, "end": v(-19.05, 45.1) * mm});
            skLineSegment(sketch, "E383", {"start": v(-19.05, 45.1) * mm, "end": v(-19.23, 45.33) * mm});
            skLineSegment(sketch, "E384", {"start": v(-19.23, 45.33) * mm, "end": v(-19.44, 45.57) * mm});
            skLineSegment(sketch, "E385", {"start": v(-19.44, 45.57) * mm, "end": v(-19.67, 45.83) * mm});
            skLineSegment(sketch, "E386", {"start": v(-19.67, 45.83) * mm, "end": v(-19.92, 46.1) * mm});
            skLineSegment(sketch, "E387", {"start": v(-19.92, 46.1) * mm, "end": v(-20.2, 46.38) * mm});
            skLineSegment(sketch, "E388", {"start": v(-20.2, 46.38) * mm, "end": v(-20.48, 46.66) * mm});
            skLineSegment(sketch, "E389", {"start": v(-20.48, 46.66) * mm, "end": v(-20.8, 46.96) * mm});
            skLineSegment(sketch, "E390", {"start": v(-20.8, 46.96) * mm, "end": v(-21.13, 47.27) * mm});
            skLineSegment(sketch, "E391", {"start": v(-21.13, 47.27) * mm, "end": v(-21.5, 47.58) * mm});
            skLineSegment(sketch, "E392", {"start": v(-21.5, 47.58) * mm, "end": v(-21.88, 47.9) * mm});
            skLineSegment(sketch, "E393", {"start": v(-21.88, 47.9) * mm, "end": v(-22.3, 48.22) * mm});
            skLineSegment(sketch, "E394", {"start": v(-22.3, 48.22) * mm, "end": v(-22.73, 48.55) * mm});
            skLineSegment(sketch, "E395", {"start": v(-22.73, 48.55) * mm, "end": v(-23.19, 48.88) * mm});
            skLineSegment(sketch, "E396", {"start": v(-23.19, 48.88) * mm, "end": v(-23.67, 49.22) * mm});
            skLineSegment(sketch, "E397", {"start": v(-23.67, 49.22) * mm, "end": v(-24.18, 49.56) * mm});
            skLineSegment(sketch, "E398", {"start": v(-24.18, 49.56) * mm, "end": v(-24.72, 49.9) * mm});
            skLineSegment(sketch, "E399", {"start": v(-24.72, 49.9) * mm, "end": v(-25.29, 50.23) * mm});
            skLineSegment(sketch, "E400", {"start": v(-25.29, 50.23) * mm, "end": v(-25.88, 50.57) * mm});
            skLineSegment(sketch, "E401", {"start": v(-25.88, 50.57) * mm, "end": v(-26.5, 50.9) * mm});
            skLineSegment(sketch, "E402", {"start": v(-26.5, 50.9) * mm, "end": v(-27.14, 51.23) * mm});
            skLineSegment(sketch, "E403", {"start": v(-27.14, 51.23) * mm, "end": v(-27.81, 51.56) * mm});
            skLineSegment(sketch, "E404", {"start": v(-27.81, 51.56) * mm, "end": v(-28.51, 51.88) * mm});
            skLineSegment(sketch, "E405", {"start": v(-28.51, 51.88) * mm, "end": v(-29.1, 51.94) * mm});
            skLineSegment(sketch, "E406", {"start": v(-29.1, 51.94) * mm, "end": v(-30.75, 50.98) * mm});
            skLineSegment(sketch, "E407", {"start": v(-30.75, 50.98) * mm, "end": v(-30.99, 50.44) * mm});
            skLineSegment(sketch, "E408", {"start": v(-30.99, 50.44) * mm, "end": v(-31.05, 49.67) * mm});
            skLineSegment(sketch, "E409", {"start": v(-31.05, 49.67) * mm, "end": v(-31.1, 48.93) * mm});
            skLineSegment(sketch, "E410", {"start": v(-31.1, 48.93) * mm, "end": v(-31.14, 48.2) * mm});
            skLineSegment(sketch, "E411", {"start": v(-31.14, 48.2) * mm, "end": v(-31.15, 47.5) * mm});
            skLineSegment(sketch, "E412", {"start": v(-31.15, 47.5) * mm, "end": v(-31.15, 46.82) * mm});
            skLineSegment(sketch, "E413", {"start": v(-31.15, 46.82) * mm, "end": v(-31.14, 46.16) * mm});
            skLineSegment(sketch, "E414", {"start": v(-31.14, 46.16) * mm, "end": v(-31.1, 45.53) * mm});
            skLineSegment(sketch, "E415", {"start": v(-31.1, 45.53) * mm, "end": v(-31.07, 44.92) * mm});
            skLineSegment(sketch, "E416", {"start": v(-31.07, 44.92) * mm, "end": v(-31.02, 44.33) * mm});
            skLineSegment(sketch, "E417", {"start": v(-31.02, 44.33) * mm, "end": v(-30.96, 43.77) * mm});
            skLineSegment(sketch, "E418", {"start": v(-30.96, 43.77) * mm, "end": v(-30.89, 43.23) * mm});
            skLineSegment(sketch, "E419", {"start": v(-30.89, 43.23) * mm, "end": v(-30.8, 42.7) * mm});
            skLineSegment(sketch, "E420", {"start": v(-30.8, 42.7) * mm, "end": v(-30.72, 42.22) * mm});
            skLineSegment(sketch, "E421", {"start": v(-30.72, 42.22) * mm, "end": v(-30.63, 41.75) * mm});
            skLineSegment(sketch, "E422", {"start": v(-30.63, 41.75) * mm, "end": v(-30.53, 41.3) * mm});
            skLineSegment(sketch, "E423", {"start": v(-30.53, 41.3) * mm, "end": v(-30.43, 40.88) * mm});
            skLineSegment(sketch, "E424", {"start": v(-30.43, 40.88) * mm, "end": v(-30.32, 40.49) * mm});
            skLineSegment(sketch, "E425", {"start": v(-30.32, 40.49) * mm, "end": v(-30.21, 40.11) * mm});
            skLineSegment(sketch, "E426", {"start": v(-30.21, 40.11) * mm, "end": v(-30.1, 39.76) * mm});
            skLineSegment(sketch, "E427", {"start": v(-30.1, 39.76) * mm, "end": v(-30, 39.44) * mm});
            skLineSegment(sketch, "E428", {"start": v(-30, 39.44) * mm, "end": v(-29.88, 39.14) * mm});
            skLineSegment(sketch, "E429", {"start": v(-29.88, 39.14) * mm, "end": v(-29.77, 38.86) * mm});
            skLineSegment(sketch, "E430", {"start": v(-29.77, 38.86) * mm, "end": v(-29.67, 38.6) * mm});
            skLineSegment(sketch, "E431", {"start": v(-29.67, 38.6) * mm, "end": v(-29.57, 38.37) * mm});
            skLineSegment(sketch, "E432", {"start": v(-29.57, 38.37) * mm, "end": v(-29.47, 38.16) * mm});
            skLineSegment(sketch, "E433", {"start": v(-29.47, 38.16) * mm, "end": v(-29.38, 37.97) * mm});
            skLineSegment(sketch, "E434", {"start": v(-29.38, 37.97) * mm, "end": v(-29.3, 37.8) * mm});
            skLineSegment(sketch, "E435", {"start": v(-29.3, 37.8) * mm, "end": v(-29.21, 37.67) * mm});
            skLineSegment(sketch, "E436", {"start": v(-29.21, 37.67) * mm, "end": v(-29.14, 37.54) * mm});
            skLineSegment(sketch, "E437", {"start": v(-29.14, 37.54) * mm, "end": v(-29.08, 37.44) * mm});
            skLineSegment(sketch, "E438", {"start": v(-29.08, 37.44) * mm, "end": v(-29.03, 37.36) * mm});
            skLineSegment(sketch, "E439", {"start": v(-29.03, 37.36) * mm, "end": v(-28.99, 37.3) * mm});
            skLineSegment(sketch, "E440", {"start": v(-28.99, 37.3) * mm, "end": v(-28.96, 37.26) * mm});
            skLineSegment(sketch, "E441", {"start": v(-28.96, 37.26) * mm, "end": v(-28.94, 37.23) * mm});
            skLineSegment(sketch, "E442", {"start": v(-28.94, 37.23) * mm, "end": v(-27.8, 35.77) * mm});
            skLineSegment(sketch, "E443", {"start": v(-27.8, 35.77) * mm, "end": v(-32.04, 32.04) * mm});
            skLineSegment(sketch, "E444", {"start": v(-32.04, 32.04) * mm, "end": v(-33.34, 33.34) * mm});
            skLineSegment(sketch, "E445", {"start": v(-33.34, 33.34) * mm, "end": v(-33.37, 33.36) * mm});
            skLineSegment(sketch, "E446", {"start": v(-33.37, 33.36) * mm, "end": v(-33.4, 33.4) * mm});
            skLineSegment(sketch, "E447", {"start": v(-33.4, 33.4) * mm, "end": v(-33.46, 33.45) * mm});
            skLineSegment(sketch, "E448", {"start": v(-33.46, 33.45) * mm, "end": v(-33.53, 33.5) * mm});
            skLineSegment(sketch, "E449", {"start": v(-33.53, 33.5) * mm, "end": v(-33.63, 33.58) * mm});
            skLineSegment(sketch, "E450", {"start": v(-33.63, 33.58) * mm, "end": v(-33.74, 33.67) * mm});
            skLineSegment(sketch, "E451", {"start": v(-33.74, 33.67) * mm, "end": v(-33.87, 33.76) * mm});
            skLineSegment(sketch, "E452", {"start": v(-33.87, 33.76) * mm, "end": v(-34.03, 33.87) * mm});
            skLineSegment(sketch, "E453", {"start": v(-34.03, 33.87) * mm, "end": v(-34.2, 33.99) * mm});
            skLineSegment(sketch, "E454", {"start": v(-34.2, 33.99) * mm, "end": v(-34.4, 34.1) * mm});
            skLineSegment(sketch, "E455", {"start": v(-34.4, 34.1) * mm, "end": v(-34.61, 34.24) * mm});
            skLineSegment(sketch, "E456", {"start": v(-34.61, 34.24) * mm, "end": v(-34.85, 34.37) * mm});
            skLineSegment(sketch, "E457", {"start": v(-34.85, 34.37) * mm, "end": v(-35.12, 34.52) * mm});
            skLineSegment(sketch, "E458", {"start": v(-35.12, 34.52) * mm, "end": v(-35.4, 34.66) * mm});
            skLineSegment(sketch, "E459", {"start": v(-35.4, 34.66) * mm, "end": v(-35.71, 34.81) * mm});
            skLineSegment(sketch, "E460", {"start": v(-35.71, 34.81) * mm, "end": v(-36.04, 34.96) * mm});
            skLineSegment(sketch, "E461", {"start": v(-36.04, 34.96) * mm, "end": v(-36.4, 35.12) * mm});
            skLineSegment(sketch, "E462", {"start": v(-36.4, 35.12) * mm, "end": v(-36.78, 35.27) * mm});
            skLineSegment(sketch, "E463", {"start": v(-36.78, 35.27) * mm, "end": v(-37.18, 35.43) * mm});
            skLineSegment(sketch, "E464", {"start": v(-37.18, 35.43) * mm, "end": v(-37.61, 35.58) * mm});
            skLineSegment(sketch, "E465", {"start": v(-37.61, 35.58) * mm, "end": v(-38.07, 35.73) * mm});
            skLineSegment(sketch, "E466", {"start": v(-38.07, 35.73) * mm, "end": v(-38.55, 35.88) * mm});
            skLineSegment(sketch, "E467", {"start": v(-38.55, 35.88) * mm, "end": v(-39.05, 36.02) * mm});
            skLineSegment(sketch, "E468", {"start": v(-39.05, 36.02) * mm, "end": v(-39.58, 36.16) * mm});
            skLineSegment(sketch, "E469", {"start": v(-39.58, 36.16) * mm, "end": v(-40.13, 36.3) * mm});
            skLineSegment(sketch, "E470", {"start": v(-40.13, 36.3) * mm, "end": v(-40.7, 36.41) * mm});
            skLineSegment(sketch, "E471", {"start": v(-40.7, 36.41) * mm, "end": v(-41.3, 36.53) * mm});
            skLineSegment(sketch, "E472", {"start": v(-41.3, 36.53) * mm, "end": v(-41.93, 36.64) * mm});
            skLineSegment(sketch, "E473", {"start": v(-41.93, 36.64) * mm, "end": v(-42.58, 36.73) * mm});
            skLineSegment(sketch, "E474", {"start": v(-42.58, 36.73) * mm, "end": v(-43.26, 36.82) * mm});
            skLineSegment(sketch, "E475", {"start": v(-43.26, 36.82) * mm, "end": v(-43.96, 36.89) * mm});
            skLineSegment(sketch, "E476", {"start": v(-43.96, 36.89) * mm, "end": v(-44.68, 36.95) * mm});
            skLineSegment(sketch, "E477", {"start": v(-44.68, 36.95) * mm, "end": v(-45.43, 36.99) * mm});
            skLineSegment(sketch, "E478", {"start": v(-45.43, 36.99) * mm, "end": v(-46.2, 37.02) * mm});
            skLineSegment(sketch, "E479", {"start": v(-46.2, 37.02) * mm, "end": v(-46.76, 36.85) * mm});
            skLineSegment(sketch, "E480", {"start": v(-46.76, 36.85) * mm, "end": v(-47.91, 35.33) * mm});
            skLineSegment(sketch, "E481", {"start": v(-47.91, 35.33) * mm, "end": v(-47.93, 34.74) * mm});
            skLineSegment(sketch, "E482", {"start": v(-47.93, 34.74) * mm, "end": v(-47.7, 34) * mm});
            skLineSegment(sketch, "E483", {"start": v(-47.7, 34) * mm, "end": v(-47.46, 33.3) * mm});
            skLineSegment(sketch, "E484", {"start": v(-47.46, 33.3) * mm, "end": v(-47.21, 32.62) * mm});
            skLineSegment(sketch, "E485", {"start": v(-47.21, 32.62) * mm, "end": v(-46.96, 31.96) * mm});
            skLineSegment(sketch, "E486", {"start": v(-46.96, 31.96) * mm, "end": v(-46.7, 31.34) * mm});
            skLineSegment(sketch, "E487", {"start": v(-46.7, 31.34) * mm, "end": v(-46.43, 30.73) * mm});
            skLineSegment(sketch, "E488", {"start": v(-46.43, 30.73) * mm, "end": v(-46.16, 30.16) * mm});
            skLineSegment(sketch, "E489", {"start": v(-46.16, 30.16) * mm, "end": v(-45.9, 29.61) * mm});
            skLineSegment(sketch, "E490", {"start": v(-45.9, 29.61) * mm, "end": v(-45.62, 29.09) * mm});
            skLineSegment(sketch, "E491", {"start": v(-45.62, 29.09) * mm, "end": v(-45.35, 28.59) * mm});
            skLineSegment(sketch, "E492", {"start": v(-45.35, 28.59) * mm, "end": v(-45.08, 28.12) * mm});
            skLineSegment(sketch, "E493", {"start": v(-45.08, 28.12) * mm, "end": v(-44.8, 27.67) * mm});
            skLineSegment(sketch, "E494", {"start": v(-44.8, 27.67) * mm, "end": v(-44.54, 27.25) * mm});
            skLineSegment(sketch, "E495", {"start": v(-44.54, 27.25) * mm, "end": v(-44.27, 26.85) * mm});
            skLineSegment(sketch, "E496", {"start": v(-44.27, 26.85) * mm, "end": v(-44.01, 26.48) * mm});
            skLineSegment(sketch, "E497", {"start": v(-44.01, 26.48) * mm, "end": v(-43.75, 26.13) * mm});
            skLineSegment(sketch, "E498", {"start": v(-43.75, 26.13) * mm, "end": v(-43.5, 25.8) * mm});
            skLineSegment(sketch, "E499", {"start": v(-43.5, 25.8) * mm, "end": v(-43.26, 25.5) * mm});
            skLineSegment(sketch, "E500", {"start": v(-43.26, 25.5) * mm, "end": v(-43.03, 25.22) * mm});
            skLineSegment(sketch, "E501", {"start": v(-43.03, 25.22) * mm, "end": v(-42.8, 24.96) * mm});
            skLineSegment(sketch, "E502", {"start": v(-42.8, 24.96) * mm, "end": v(-42.58, 24.72) * mm});
            skLineSegment(sketch, "E503", {"start": v(-42.58, 24.72) * mm, "end": v(-42.38, 24.5) * mm});
            skLineSegment(sketch, "E504", {"start": v(-42.38, 24.5) * mm, "end": v(-42.18, 24.31) * mm});
            skLineSegment(sketch, "E505", {"start": v(-42.18, 24.31) * mm, "end": v(-42, 24.14) * mm});
            skLineSegment(sketch, "E506", {"start": v(-42, 24.14) * mm, "end": v(-41.83, 23.98) * mm});
            skLineSegment(sketch, "E507", {"start": v(-41.83, 23.98) * mm, "end": v(-41.67, 23.84) * mm});
            skLineSegment(sketch, "E508", {"start": v(-41.67, 23.84) * mm, "end": v(-41.53, 23.72) * mm});
            skLineSegment(sketch, "E509", {"start": v(-41.53, 23.72) * mm, "end": v(-41.4, 23.62) * mm});
            skLineSegment(sketch, "E510", {"start": v(-41.4, 23.62) * mm, "end": v(-41.29, 23.53) * mm});
            skLineSegment(sketch, "E511", {"start": v(-41.29, 23.53) * mm, "end": v(-41.2, 23.46) * mm});
            skLineSegment(sketch, "E512", {"start": v(-41.2, 23.46) * mm, "end": v(-41.12, 23.4) * mm});
            skLineSegment(sketch, "E513", {"start": v(-41.12, 23.4) * mm, "end": v(-41.05, 23.37) * mm});
            skLineSegment(sketch, "E514", {"start": v(-41.05, 23.37) * mm, "end": v(-41, 23.34) * mm});
            skLineSegment(sketch, "E515", {"start": v(-41, 23.34) * mm, "end": v(-40.98, 23.32) * mm});
            skLineSegment(sketch, "E516", {"start": v(-40.98, 23.32) * mm, "end": v(-39.38, 22.4) * mm});
            skLineSegment(sketch, "E517", {"start": v(-39.38, 22.4) * mm, "end": v(-41.86, 17.34) * mm});
            skLineSegment(sketch, "E518", {"start": v(-41.86, 17.34) * mm, "end": v(-43.57, 18.05) * mm});
            skLineSegment(sketch, "E519", {"start": v(-43.57, 18.05) * mm, "end": v(-43.6, 18.06) * mm});
            skLineSegment(sketch, "E520", {"start": v(-43.6, 18.06) * mm, "end": v(-43.64, 18.07) * mm});
            skLineSegment(sketch, "E521", {"start": v(-43.64, 18.07) * mm, "end": v(-43.71, 18.1) * mm});
            skLineSegment(sketch, "E522", {"start": v(-43.71, 18.1) * mm, "end": v(-43.8, 18.13) * mm});
            skLineSegment(sketch, "E523", {"start": v(-43.8, 18.13) * mm, "end": v(-43.92, 18.16) * mm});
            skLineSegment(sketch, "E524", {"start": v(-43.92, 18.16) * mm, "end": v(-44.06, 18.2) * mm});
            skLineSegment(sketch, "E525", {"start": v(-44.06, 18.2) * mm, "end": v(-44.22, 18.23) * mm});
            skLineSegment(sketch, "E526", {"start": v(-44.22, 18.23) * mm, "end": v(-44.4, 18.27) * mm});
            skLineSegment(sketch, "E527", {"start": v(-44.4, 18.27) * mm, "end": v(-44.6, 18.3) * mm});
            skLineSegment(sketch, "E528", {"start": v(-44.6, 18.3) * mm, "end": v(-44.83, 18.35) * mm});
            skLineSegment(sketch, "E529", {"start": v(-44.83, 18.35) * mm, "end": v(-45.08, 18.39) * mm});
            skLineSegment(sketch, "E530", {"start": v(-45.08, 18.39) * mm, "end": v(-45.36, 18.42) * mm});
            skLineSegment(sketch, "E531", {"start": v(-45.36, 18.42) * mm, "end": v(-45.65, 18.45) * mm});
            skLineSegment(sketch, "E532", {"start": v(-45.65, 18.45) * mm, "end": v(-45.97, 18.48) * mm});
            skLineSegment(sketch, "E533", {"start": v(-45.97, 18.48) * mm, "end": v(-46.31, 18.5) * mm});
            skLineSegment(sketch, "E534", {"start": v(-46.31, 18.5) * mm, "end": v(-46.68, 18.51) * mm});
            skLineSegment(sketch, "E535", {"start": v(-46.68, 18.51) * mm, "end": v(-47.07, 18.52) * mm});
            skLineSegment(sketch, "E536", {"start": v(-47.07, 18.52) * mm, "end": v(-47.48, 18.51) * mm});
            skLineSegment(sketch, "E537", {"start": v(-47.48, 18.51) * mm, "end": v(-47.91, 18.5) * mm});
            skLineSegment(sketch, "E538", {"start": v(-47.91, 18.5) * mm, "end": v(-48.37, 18.48) * mm});
            skLineSegment(sketch, "E539", {"start": v(-48.37, 18.48) * mm, "end": v(-48.84, 18.44) * mm});
            skLineSegment(sketch, "E540", {"start": v(-48.84, 18.44) * mm, "end": v(-49.34, 18.4) * mm});
            skLineSegment(sketch, "E541", {"start": v(-49.34, 18.4) * mm, "end": v(-49.86, 18.34) * mm});
            skLineSegment(sketch, "E542", {"start": v(-49.86, 18.34) * mm, "end": v(-50.4, 18.26) * mm});
            skLineSegment(sketch, "E543", {"start": v(-50.4, 18.26) * mm, "end": v(-50.96, 18.17) * mm});
            skLineSegment(sketch, "E544", {"start": v(-50.96, 18.17) * mm, "end": v(-51.54, 18.06) * mm});
            skLineSegment(sketch, "E545", {"start": v(-51.54, 18.06) * mm, "end": v(-52.14, 17.94) * mm});
            skLineSegment(sketch, "E546", {"start": v(-52.14, 17.94) * mm, "end": v(-52.76, 17.8) * mm});
            skLineSegment(sketch, "E547", {"start": v(-52.76, 17.8) * mm, "end": v(-53.4, 17.64) * mm});
            skLineSegment(sketch, "E548", {"start": v(-53.4, 17.64) * mm, "end": v(-54.05, 17.46) * mm});
            skLineSegment(sketch, "E549", {"start": v(-54.05, 17.46) * mm, "end": v(-54.73, 17.26) * mm});
            skLineSegment(sketch, "E550", {"start": v(-54.73, 17.26) * mm, "end": v(-55.42, 17.04) * mm});
            skLineSegment(sketch, "E551", {"start": v(-55.42, 17.04) * mm, "end": v(-56.12, 16.8) * mm});
            skLineSegment(sketch, "E552", {"start": v(-56.12, 16.8) * mm, "end": v(-56.85, 16.52) * mm});
            skLineSegment(sketch, "E553", {"start": v(-56.85, 16.52) * mm, "end": v(-57.3, 16.15) * mm});
            skLineSegment(sketch, "E554", {"start": v(-57.3, 16.15) * mm, "end": v(-57.79, 14.3) * mm});
            skLineSegment(sketch, "E555", {"start": v(-57.79, 14.3) * mm, "end": v(-57.58, 13.76) * mm});
            skLineSegment(sketch, "E556", {"start": v(-57.58, 13.76) * mm, "end": v(-57.08, 13.17) * mm});
            skLineSegment(sketch, "E557", {"start": v(-57.08, 13.17) * mm, "end": v(-56.6, 12.6) * mm});
            skLineSegment(sketch, "E558", {"start": v(-56.6, 12.6) * mm, "end": v(-56.1, 12.07) * mm});
            skLineSegment(sketch, "E559", {"start": v(-56.1, 12.07) * mm, "end": v(-55.62, 11.56) * mm});
            skLineSegment(sketch, "E560", {"start": v(-55.62, 11.56) * mm, "end": v(-55.14, 11.08) * mm});
            skLineSegment(sketch, "E561", {"start": v(-55.14, 11.08) * mm, "end": v(-54.66, 10.63) * mm});
            skLineSegment(sketch, "E562", {"start": v(-54.66, 10.63) * mm, "end": v(-54.2, 10.2) * mm});
            skLineSegment(sketch, "E563", {"start": v(-54.2, 10.2) * mm, "end": v(-53.73, 9.8) * mm});
            skLineSegment(sketch, "E564", {"start": v(-53.73, 9.8) * mm, "end": v(-53.28, 9.41) * mm});
            skLineSegment(sketch, "E565", {"start": v(-53.28, 9.41) * mm, "end": v(-52.84, 9.06) * mm});
            skLineSegment(sketch, "E566", {"start": v(-52.84, 9.06) * mm, "end": v(-52.4, 8.73) * mm});
            skLineSegment(sketch, "E567", {"start": v(-52.4, 8.73) * mm, "end": v(-51.98, 8.42) * mm});
            skLineSegment(sketch, "E568", {"start": v(-51.98, 8.42) * mm, "end": v(-51.57, 8.13) * mm});
            skLineSegment(sketch, "E569", {"start": v(-51.57, 8.13) * mm, "end": v(-51.18, 7.86) * mm});
            skLineSegment(sketch, "E570", {"start": v(-51.18, 7.86) * mm, "end": v(-50.8, 7.62) * mm});
            skLineSegment(sketch, "E571", {"start": v(-50.8, 7.62) * mm, "end": v(-50.42, 7.4) * mm});
            skLineSegment(sketch, "E572", {"start": v(-50.42, 7.4) * mm, "end": v(-50.07, 7.19) * mm});
            skLineSegment(sketch, "E573", {"start": v(-50.07, 7.19) * mm, "end": v(-49.73, 7) * mm});
            skLineSegment(sketch, "E574", {"start": v(-49.73, 7) * mm, "end": v(-49.4, 6.83) * mm});
            skLineSegment(sketch, "E575", {"start": v(-49.4, 6.83) * mm, "end": v(-49.1, 6.68) * mm});
            skLineSegment(sketch, "E576", {"start": v(-49.1, 6.68) * mm, "end": v(-48.8, 6.54) * mm});
            skLineSegment(sketch, "E577", {"start": v(-48.8, 6.54) * mm, "end": v(-48.53, 6.42) * mm});
            skLineSegment(sketch, "E578", {"start": v(-48.53, 6.42) * mm, "end": v(-48.27, 6.32) * mm});
            skLineSegment(sketch, "E579", {"start": v(-48.27, 6.32) * mm, "end": v(-48.04, 6.23) * mm});
            skLineSegment(sketch, "E580", {"start": v(-48.04, 6.23) * mm, "end": v(-47.82, 6.15) * mm});
            skLineSegment(sketch, "E581", {"start": v(-47.82, 6.15) * mm, "end": v(-47.62, 6.08) * mm});
            skLineSegment(sketch, "E582", {"start": v(-47.62, 6.08) * mm, "end": v(-47.45, 6.02) * mm});
            skLineSegment(sketch, "E583", {"start": v(-47.45, 6.02) * mm, "end": v(-47.29, 5.98) * mm});
            skLineSegment(sketch, "E584", {"start": v(-47.29, 5.98) * mm, "end": v(-47.15, 5.94) * mm});
            skLineSegment(sketch, "E585", {"start": v(-47.15, 5.94) * mm, "end": v(-47.04, 5.91) * mm});
            skLineSegment(sketch, "E586", {"start": v(-47.04, 5.91) * mm, "end": v(-46.94, 5.9) * mm});
            skLineSegment(sketch, "E587", {"start": v(-46.94, 5.9) * mm, "end": v(-46.87, 5.88) * mm});
            skLineSegment(sketch, "E588", {"start": v(-46.87, 5.88) * mm, "end": v(-46.82, 5.87) * mm});
            skLineSegment(sketch, "E589", {"start": v(-46.82, 5.87) * mm, "end": v(-46.79, 5.86) * mm});
            skLineSegment(sketch, "E590", {"start": v(-46.79, 5.86) * mm, "end": v(-44.96, 5.64) * mm});
            skLineSegment(sketch, "E591", {"start": v(-44.96, 5.64) * mm, "end": v(-45.3, 0) * mm});
            skLineSegment(sketch, "E592", {"start": v(-45.3, 0) * mm, "end": v(-47.16, 0) * mm});
            skLineSegment(sketch, "E593", {"start": v(-47.16, 0) * mm, "end": v(-47.19, 0) * mm});
            skLineSegment(sketch, "E594", {"start": v(-47.19, 0) * mm, "end": v(-47.24, 0) * mm});
            skLineSegment(sketch, "E595", {"start": v(-47.24, 0) * mm, "end": v(-47.31, 0) * mm});
            skLineSegment(sketch, "E596", {"start": v(-47.31, 0) * mm, "end": v(-47.4, -0.02) * mm});
            skLineSegment(sketch, "E597", {"start": v(-47.4, -0.02) * mm, "end": v(-47.52, -0.03) * mm});
            skLineSegment(sketch, "E598", {"start": v(-47.52, -0.03) * mm, "end": v(-47.66, -0.05) * mm});
            skLineSegment(sketch, "E599", {"start": v(-47.66, -0.05) * mm, "end": v(-47.83, -0.08) * mm});
            skLineSegment(sketch, "E600", {"start": v(-47.83, -0.08) * mm, "end": v(-48, -0.1) * mm});
            skLineSegment(sketch, "E601", {"start": v(-48, -0.1) * mm, "end": v(-48.21, -0.15) * mm});
            skLineSegment(sketch, "E602", {"start": v(-48.21, -0.15) * mm, "end": v(-48.44, -0.2) * mm});
            skLineSegment(sketch, "E603", {"start": v(-48.44, -0.2) * mm, "end": v(-48.69, -0.27) * mm});
            skLineSegment(sketch, "E604", {"start": v(-48.69, -0.27) * mm, "end": v(-48.95, -0.34) * mm});
            skLineSegment(sketch, "E605", {"start": v(-48.95, -0.34) * mm, "end": v(-49.24, -0.42) * mm});
            skLineSegment(sketch, "E606", {"start": v(-49.24, -0.42) * mm, "end": v(-49.54, -0.52) * mm});
            skLineSegment(sketch, "E607", {"start": v(-49.54, -0.52) * mm, "end": v(-49.87, -0.64) * mm});
            skLineSegment(sketch, "E608", {"start": v(-49.87, -0.64) * mm, "end": v(-50.21, -0.76) * mm});
            skLineSegment(sketch, "E609", {"start": v(-50.21, -0.76) * mm, "end": v(-50.57, -0.9) * mm});
            skLineSegment(sketch, "E610", {"start": v(-50.57, -0.9) * mm, "end": v(-50.95, -1.07) * mm});
            skLineSegment(sketch, "E611", {"start": v(-50.95, -1.07) * mm, "end": v(-51.34, -1.24) * mm});
            skLineSegment(sketch, "E612", {"start": v(-51.34, -1.24) * mm, "end": v(-51.76, -1.44) * mm});
            skLineSegment(sketch, "E613", {"start": v(-51.76, -1.44) * mm, "end": v(-52.18, -1.65) * mm});
            skLineSegment(sketch, "E614", {"start": v(-52.18, -1.65) * mm, "end": v(-52.63, -1.89) * mm});
            skLineSegment(sketch, "E615", {"start": v(-52.63, -1.89) * mm, "end": v(-53.08, -2.14) * mm});
            skLineSegment(sketch, "E616", {"start": v(-53.08, -2.14) * mm, "end": v(-53.55, -2.42) * mm});
            skLineSegment(sketch, "E617", {"start": v(-53.55, -2.42) * mm, "end": v(-54.04, -2.71) * mm});
            skLineSegment(sketch, "E618", {"start": v(-54.04, -2.71) * mm, "end": v(-54.53, -3.04) * mm});
            skLineSegment(sketch, "E619", {"start": v(-54.53, -3.04) * mm, "end": v(-55.04, -3.38) * mm});
            skLineSegment(sketch, "E620", {"start": v(-55.04, -3.38) * mm, "end": v(-55.56, -3.75) * mm});
            skLineSegment(sketch, "E621", {"start": v(-55.56, -3.75) * mm, "end": v(-56.08, -4.14) * mm});
            skLineSegment(sketch, "E622", {"start": v(-56.08, -4.14) * mm, "end": v(-56.62, -4.56) * mm});
            skLineSegment(sketch, "E623", {"start": v(-56.62, -4.56) * mm, "end": v(-57.17, -5) * mm});
            skLineSegment(sketch, "E624", {"start": v(-57.17, -5) * mm, "end": v(-57.72, -5.47) * mm});
            skLineSegment(sketch, "E625", {"start": v(-57.72, -5.47) * mm, "end": v(-58.28, -5.97) * mm});
            skLineSegment(sketch, "E626", {"start": v(-58.28, -5.97) * mm, "end": v(-58.84, -6.49) * mm});
            skLineSegment(sketch, "E627", {"start": v(-58.84, -6.49) * mm, "end": v(-59.12, -7) * mm});
            skLineSegment(sketch, "E628", {"start": v(-59.12, -7) * mm, "end": v(-58.86, -8.9) * mm});
            skLineSegment(sketch, "E629", {"start": v(-58.86, -8.9) * mm, "end": v(-58.46, -9.33) * mm});
            skLineSegment(sketch, "E630", {"start": v(-58.46, -9.33) * mm, "end": v(-57.78, -9.68) * mm});
            skLineSegment(sketch, "E631", {"start": v(-57.78, -9.68) * mm, "end": v(-57.1, -10.01) * mm});
            skLineSegment(sketch, "E632", {"start": v(-57.1, -10.01) * mm, "end": v(-56.45, -10.32) * mm});
            skLineSegment(sketch, "E633", {"start": v(-56.45, -10.32) * mm, "end": v(-55.8, -10.6) * mm});
            skLineSegment(sketch, "E634", {"start": v(-55.8, -10.6) * mm, "end": v(-55.18, -10.86) * mm});
            skLineSegment(sketch, "E635", {"start": v(-55.18, -10.86) * mm, "end": v(-54.57, -11.1) * mm});
            skLineSegment(sketch, "E636", {"start": v(-54.57, -11.1) * mm, "end": v(-53.97, -11.32) * mm});
            skLineSegment(sketch, "E637", {"start": v(-53.97, -11.32) * mm, "end": v(-53.39, -11.52) * mm});
            skLineSegment(sketch, "E638", {"start": v(-53.39, -11.52) * mm, "end": v(-52.83, -11.7) * mm});
            skLineSegment(sketch, "E639", {"start": v(-52.83, -11.7) * mm, "end": v(-52.28, -11.85) * mm});
            skLineSegment(sketch, "E640", {"start": v(-52.28, -11.85) * mm, "end": v(-51.75, -12) * mm});
            skLineSegment(sketch, "E641", {"start": v(-51.75, -12) * mm, "end": v(-51.25, -12.12) * mm});
            skLineSegment(sketch, "E642", {"start": v(-51.25, -12.12) * mm, "end": v(-50.76, -12.23) * mm});
            skLineSegment(sketch, "E643", {"start": v(-50.76, -12.23) * mm, "end": v(-50.3, -12.32) * mm});
            skLineSegment(sketch, "E644", {"start": v(-50.3, -12.32) * mm, "end": v(-49.84, -12.4) * mm});
            skLineSegment(sketch, "E645", {"start": v(-49.84, -12.4) * mm, "end": v(-49.41, -12.46) * mm});
            skLineSegment(sketch, "E646", {"start": v(-49.41, -12.46) * mm, "end": v(-49, -12.52) * mm});
            skLineSegment(sketch, "E647", {"start": v(-49, -12.52) * mm, "end": v(-48.62, -12.56) * mm});
            skLineSegment(sketch, "E648", {"start": v(-48.62, -12.56) * mm, "end": v(-48.26, -12.6) * mm});
            skLineSegment(sketch, "E649", {"start": v(-48.26, -12.6) * mm, "end": v(-47.91, -12.62) * mm});
            skLineSegment(sketch, "E650", {"start": v(-47.91, -12.62) * mm, "end": v(-47.6, -12.63) * mm});
            skLineSegment(sketch, "E651", {"start": v(-47.6, -12.63) * mm, "end": v(-47.3, -12.64) * mm});
            skLineSegment(sketch, "E652", {"start": v(-47.3, -12.64) * mm, "end": v(-47.02, -12.64) * mm});
            skLineSegment(sketch, "E653", {"start": v(-47.02, -12.64) * mm, "end": v(-46.76, -12.63) * mm});
            skLineSegment(sketch, "E654", {"start": v(-46.76, -12.63) * mm, "end": v(-46.53, -12.62) * mm});
            skLineSegment(sketch, "E655", {"start": v(-46.53, -12.62) * mm, "end": v(-46.33, -12.6) * mm});
            skLineSegment(sketch, "E656", {"start": v(-46.33, -12.6) * mm, "end": v(-46.14, -12.6) * mm});
            skLineSegment(sketch, "E657", {"start": v(-46.14, -12.6) * mm, "end": v(-45.98, -12.57) * mm});
            skLineSegment(sketch, "E658", {"start": v(-45.98, -12.57) * mm, "end": v(-45.84, -12.56) * mm});
            skLineSegment(sketch, "E659", {"start": v(-45.84, -12.56) * mm, "end": v(-45.72, -12.54) * mm});
            skLineSegment(sketch, "E660", {"start": v(-45.72, -12.54) * mm, "end": v(-45.62, -12.52) * mm});
            skLineSegment(sketch, "E661", {"start": v(-45.62, -12.52) * mm, "end": v(-45.55, -12.5) * mm});
            skLineSegment(sketch, "E662", {"start": v(-45.55, -12.5) * mm, "end": v(-45.5, -12.5) * mm});
            skLineSegment(sketch, "E663", {"start": v(-45.5, -12.5) * mm, "end": v(-45.47, -12.49) * mm});
            skLineSegment(sketch, "E664", {"start": v(-45.47, -12.49) * mm, "end": v(-43.7, -12) * mm});
            skLineSegment(sketch, "E665", {"start": v(-43.7, -12) * mm, "end": v(-41.86, -17.34) * mm});
            skLineSegment(sketch, "E666", {"start": v(-41.86, -17.34) * mm, "end": v(-43.57, -18.05) * mm});
            skLineSegment(sketch, "E667", {"start": v(-43.57, -18.05) * mm, "end": v(-43.6, -18.06) * mm});
            skLineSegment(sketch, "E668", {"start": v(-43.6, -18.06) * mm, "end": v(-43.64, -18.08) * mm});
            skLineSegment(sketch, "E669", {"start": v(-43.64, -18.08) * mm, "end": v(-43.7, -18.11) * mm});
            skLineSegment(sketch, "E670", {"start": v(-43.7, -18.11) * mm, "end": v(-43.8, -18.16) * mm});
            skLineSegment(sketch, "E671", {"start": v(-43.8, -18.16) * mm, "end": v(-43.9, -18.22) * mm});
            skLineSegment(sketch, "E672", {"start": v(-43.9, -18.22) * mm, "end": v(-44.02, -18.29) * mm});
            skLineSegment(sketch, "E673", {"start": v(-44.02, -18.29) * mm, "end": v(-44.16, -18.37) * mm});
            skLineSegment(sketch, "E674", {"start": v(-44.16, -18.37) * mm, "end": v(-44.31, -18.48) * mm});
            skLineSegment(sketch, "E675", {"start": v(-44.31, -18.48) * mm, "end": v(-44.49, -18.6) * mm});
            skLineSegment(sketch, "E676", {"start": v(-44.49, -18.6) * mm, "end": v(-44.67, -18.73) * mm});
            skLineSegment(sketch, "E677", {"start": v(-44.67, -18.73) * mm, "end": v(-44.88, -18.88) * mm});
            skLineSegment(sketch, "E678", {"start": v(-44.88, -18.88) * mm, "end": v(-45.1, -19.05) * mm});
            skLineSegment(sketch, "E679", {"start": v(-45.1, -19.05) * mm, "end": v(-45.33, -19.23) * mm});
            skLineSegment(sketch, "E680", {"start": v(-45.33, -19.23) * mm, "end": v(-45.57, -19.44) * mm});
            skLineSegment(sketch, "E681", {"start": v(-45.57, -19.44) * mm, "end": v(-45.83, -19.67) * mm});
            skLineSegment(sketch, "E682", {"start": v(-45.83, -19.67) * mm, "end": v(-46.1, -19.92) * mm});
            skLineSegment(sketch, "E683", {"start": v(-46.1, -19.92) * mm, "end": v(-46.38, -20.2) * mm});
            skLineSegment(sketch, "E684", {"start": v(-46.38, -20.2) * mm, "end": v(-46.66, -20.48) * mm});
            skLineSegment(sketch, "E685", {"start": v(-46.66, -20.48) * mm, "end": v(-46.96, -20.8) * mm});
            skLineSegment(sketch, "E686", {"start": v(-46.96, -20.8) * mm, "end": v(-47.27, -21.13) * mm});
            skLineSegment(sketch, "E687", {"start": v(-47.27, -21.13) * mm, "end": v(-47.58, -21.5) * mm});
            skLineSegment(sketch, "E688", {"start": v(-47.58, -21.5) * mm, "end": v(-47.9, -21.88) * mm});
            skLineSegment(sketch, "E689", {"start": v(-47.9, -21.88) * mm, "end": v(-48.22, -22.3) * mm});
            skLineSegment(sketch, "E690", {"start": v(-48.22, -22.3) * mm, "end": v(-48.55, -22.73) * mm});
            skLineSegment(sketch, "E691", {"start": v(-48.55, -22.73) * mm, "end": v(-48.88, -23.19) * mm});
            skLineSegment(sketch, "E692", {"start": v(-48.88, -23.19) * mm, "end": v(-49.22, -23.67) * mm});
            skLineSegment(sketch, "E693", {"start": v(-49.22, -23.67) * mm, "end": v(-49.56, -24.18) * mm});
            skLineSegment(sketch, "E694", {"start": v(-49.56, -24.18) * mm, "end": v(-49.9, -24.72) * mm});
            skLineSegment(sketch, "E695", {"start": v(-49.9, -24.72) * mm, "end": v(-50.23, -25.29) * mm});
            skLineSegment(sketch, "E696", {"start": v(-50.23, -25.29) * mm, "end": v(-50.57, -25.88) * mm});
            skLineSegment(sketch, "E697", {"start": v(-50.57, -25.88) * mm, "end": v(-50.9, -26.5) * mm});
            skLineSegment(sketch, "E698", {"start": v(-50.9, -26.5) * mm, "end": v(-51.23, -27.14) * mm});
            skLineSegment(sketch, "E699", {"start": v(-51.23, -27.14) * mm, "end": v(-51.56, -27.81) * mm});
            skLineSegment(sketch, "E700", {"start": v(-51.56, -27.81) * mm, "end": v(-51.88, -28.51) * mm});
            skLineSegment(sketch, "E701", {"start": v(-51.88, -28.51) * mm, "end": v(-51.94, -29.1) * mm});
            skLineSegment(sketch, "E702", {"start": v(-51.94, -29.1) * mm, "end": v(-50.98, -30.75) * mm});
            skLineSegment(sketch, "E703", {"start": v(-50.98, -30.75) * mm, "end": v(-50.44, -30.99) * mm});
            skLineSegment(sketch, "E704", {"start": v(-50.44, -30.99) * mm, "end": v(-49.67, -31.05) * mm});
            skLineSegment(sketch, "E705", {"start": v(-49.67, -31.05) * mm, "end": v(-48.93, -31.1) * mm});
            skLineSegment(sketch, "E706", {"start": v(-48.93, -31.1) * mm, "end": v(-48.2, -31.14) * mm});
            skLineSegment(sketch, "E707", {"start": v(-48.2, -31.14) * mm, "end": v(-47.5, -31.15) * mm});
            skLineSegment(sketch, "E708", {"start": v(-47.5, -31.15) * mm, "end": v(-46.82, -31.15) * mm});
            skLineSegment(sketch, "E709", {"start": v(-46.82, -31.15) * mm, "end": v(-46.16, -31.14) * mm});
            skLineSegment(sketch, "E710", {"start": v(-46.16, -31.14) * mm, "end": v(-45.53, -31.1) * mm});
            skLineSegment(sketch, "E711", {"start": v(-45.53, -31.1) * mm, "end": v(-44.92, -31.07) * mm});
            skLineSegment(sketch, "E712", {"start": v(-44.92, -31.07) * mm, "end": v(-44.33, -31.02) * mm});
            skLineSegment(sketch, "E713", {"start": v(-44.33, -31.02) * mm, "end": v(-43.77, -30.96) * mm});
            skLineSegment(sketch, "E714", {"start": v(-43.77, -30.96) * mm, "end": v(-43.23, -30.89) * mm});
            skLineSegment(sketch, "E715", {"start": v(-43.23, -30.89) * mm, "end": v(-42.7, -30.8) * mm});
            skLineSegment(sketch, "E716", {"start": v(-42.7, -30.8) * mm, "end": v(-42.22, -30.72) * mm});
            skLineSegment(sketch, "E717", {"start": v(-42.22, -30.72) * mm, "end": v(-41.75, -30.63) * mm});
            skLineSegment(sketch, "E718", {"start": v(-41.75, -30.63) * mm, "end": v(-41.3, -30.53) * mm});
            skLineSegment(sketch, "E719", {"start": v(-41.3, -30.53) * mm, "end": v(-40.88, -30.43) * mm});
            skLineSegment(sketch, "E720", {"start": v(-40.88, -30.43) * mm, "end": v(-40.49, -30.32) * mm});
            skLineSegment(sketch, "E721", {"start": v(-40.49, -30.32) * mm, "end": v(-40.11, -30.21) * mm});
            skLineSegment(sketch, "E722", {"start": v(-40.11, -30.21) * mm, "end": v(-39.76, -30.1) * mm});
            skLineSegment(sketch, "E723", {"start": v(-39.76, -30.1) * mm, "end": v(-39.44, -30) * mm});
            skLineSegment(sketch, "E724", {"start": v(-39.44, -30) * mm, "end": v(-39.14, -29.88) * mm});
            skLineSegment(sketch, "E725", {"start": v(-39.14, -29.88) * mm, "end": v(-38.86, -29.77) * mm});
            skLineSegment(sketch, "E726", {"start": v(-38.86, -29.77) * mm, "end": v(-38.6, -29.67) * mm});
            skLineSegment(sketch, "E727", {"start": v(-38.6, -29.67) * mm, "end": v(-38.37, -29.57) * mm});
            skLineSegment(sketch, "E728", {"start": v(-38.37, -29.57) * mm, "end": v(-38.16, -29.47) * mm});
            skLineSegment(sketch, "E729", {"start": v(-38.16, -29.47) * mm, "end": v(-37.97, -29.38) * mm});
            skLineSegment(sketch, "E730", {"start": v(-37.97, -29.38) * mm, "end": v(-37.8, -29.3) * mm});
            skLineSegment(sketch, "E731", {"start": v(-37.8, -29.3) * mm, "end": v(-37.67, -29.21) * mm});
            skLineSegment(sketch, "E732", {"start": v(-37.67, -29.21) * mm, "end": v(-37.54, -29.14) * mm});
            skLineSegment(sketch, "E733", {"start": v(-37.54, -29.14) * mm, "end": v(-37.44, -29.08) * mm});
            skLineSegment(sketch, "E734", {"start": v(-37.44, -29.08) * mm, "end": v(-37.36, -29.03) * mm});
            skLineSegment(sketch, "E735", {"start": v(-37.36, -29.03) * mm, "end": v(-37.3, -28.99) * mm});
            skLineSegment(sketch, "E736", {"start": v(-37.3, -28.99) * mm, "end": v(-37.26, -28.96) * mm});
            skLineSegment(sketch, "E737", {"start": v(-37.26, -28.96) * mm, "end": v(-37.23, -28.94) * mm});
            skLineSegment(sketch, "E738", {"start": v(-37.23, -28.94) * mm, "end": v(-35.77, -27.8) * mm});
            skLineSegment(sketch, "E739", {"start": v(-35.77, -27.8) * mm, "end": v(-32.04, -32.04) * mm});
            skLineSegment(sketch, "E740", {"start": v(-32.04, -32.04) * mm, "end": v(-33.34, -33.34) * mm});
            skLineSegment(sketch, "E741", {"start": v(-33.34, -33.34) * mm, "end": v(-33.36, -33.37) * mm});
            skLineSegment(sketch, "E742", {"start": v(-33.36, -33.37) * mm, "end": v(-33.4, -33.4) * mm});
            skLineSegment(sketch, "E743", {"start": v(-33.4, -33.4) * mm, "end": v(-33.45, -33.46) * mm});
            skLineSegment(sketch, "E744", {"start": v(-33.45, -33.46) * mm, "end": v(-33.5, -33.53) * mm});
            skLineSegment(sketch, "E745", {"start": v(-33.5, -33.53) * mm, "end": v(-33.58, -33.63) * mm});
            skLineSegment(sketch, "E746", {"start": v(-33.58, -33.63) * mm, "end": v(-33.67, -33.74) * mm});
            skLineSegment(sketch, "E747", {"start": v(-33.67, -33.74) * mm, "end": v(-33.76, -33.87) * mm});
            skLineSegment(sketch, "E748", {"start": v(-33.76, -33.87) * mm, "end": v(-33.87, -34.03) * mm});
            skLineSegment(sketch, "E749", {"start": v(-33.87, -34.03) * mm, "end": v(-33.99, -34.2) * mm});
            skLineSegment(sketch, "E750", {"start": v(-33.99, -34.2) * mm, "end": v(-34.1, -34.4) * mm});
            skLineSegment(sketch, "E751", {"start": v(-34.1, -34.4) * mm, "end": v(-34.24, -34.61) * mm});
            skLineSegment(sketch, "E752", {"start": v(-34.24, -34.61) * mm, "end": v(-34.37, -34.85) * mm});
            skLineSegment(sketch, "E753", {"start": v(-34.37, -34.85) * mm, "end": v(-34.52, -35.12) * mm});
            skLineSegment(sketch, "E754", {"start": v(-34.52, -35.12) * mm, "end": v(-34.66, -35.4) * mm});
            skLineSegment(sketch, "E755", {"start": v(-34.66, -35.4) * mm, "end": v(-34.81, -35.71) * mm});
            skLineSegment(sketch, "E756", {"start": v(-34.81, -35.71) * mm, "end": v(-34.96, -36.04) * mm});
            skLineSegment(sketch, "E757", {"start": v(-34.96, -36.04) * mm, "end": v(-35.12, -36.4) * mm});
            skLineSegment(sketch, "E758", {"start": v(-35.12, -36.4) * mm, "end": v(-35.27, -36.78) * mm});
            skLineSegment(sketch, "E759", {"start": v(-35.27, -36.78) * mm, "end": v(-35.43, -37.18) * mm});
            skLineSegment(sketch, "E760", {"start": v(-35.43, -37.18) * mm, "end": v(-35.58, -37.61) * mm});
            skLineSegment(sketch, "E761", {"start": v(-35.58, -37.61) * mm, "end": v(-35.73, -38.07) * mm});
            skLineSegment(sketch, "E762", {"start": v(-35.73, -38.07) * mm, "end": v(-35.88, -38.55) * mm});
            skLineSegment(sketch, "E763", {"start": v(-35.88, -38.55) * mm, "end": v(-36.02, -39.05) * mm});
            skLineSegment(sketch, "E764", {"start": v(-36.02, -39.05) * mm, "end": v(-36.16, -39.58) * mm});
            skLineSegment(sketch, "E765", {"start": v(-36.16, -39.58) * mm, "end": v(-36.3, -40.13) * mm});
            skLineSegment(sketch, "E766", {"start": v(-36.3, -40.13) * mm, "end": v(-36.41, -40.7) * mm});
            skLineSegment(sketch, "E767", {"start": v(-36.41, -40.7) * mm, "end": v(-36.53, -41.3) * mm});
            skLineSegment(sketch, "E768", {"start": v(-36.53, -41.3) * mm, "end": v(-36.64, -41.93) * mm});
            skLineSegment(sketch, "E769", {"start": v(-36.64, -41.93) * mm, "end": v(-36.73, -42.58) * mm});
            skLineSegment(sketch, "E770", {"start": v(-36.73, -42.58) * mm, "end": v(-36.82, -43.26) * mm});
            skLineSegment(sketch, "E771", {"start": v(-36.82, -43.26) * mm, "end": v(-36.89, -43.96) * mm});
            skLineSegment(sketch, "E772", {"start": v(-36.89, -43.96) * mm, "end": v(-36.95, -44.68) * mm});
            skLineSegment(sketch, "E773", {"start": v(-36.95, -44.68) * mm, "end": v(-36.99, -45.43) * mm});
            skLineSegment(sketch, "E774", {"start": v(-36.99, -45.43) * mm, "end": v(-37.02, -46.2) * mm});
            skLineSegment(sketch, "E775", {"start": v(-37.02, -46.2) * mm, "end": v(-36.85, -46.76) * mm});
            skLineSegment(sketch, "E776", {"start": v(-36.85, -46.76) * mm, "end": v(-35.33, -47.91) * mm});
            skLineSegment(sketch, "E777", {"start": v(-35.33, -47.91) * mm, "end": v(-34.74, -47.93) * mm});
            skLineSegment(sketch, "E778", {"start": v(-34.74, -47.93) * mm, "end": v(-34, -47.7) * mm});
            skLineSegment(sketch, "E779", {"start": v(-34, -47.7) * mm, "end": v(-33.3, -47.46) * mm});
            skLineSegment(sketch, "E780", {"start": v(-33.3, -47.46) * mm, "end": v(-32.62, -47.21) * mm});
            skLineSegment(sketch, "E781", {"start": v(-32.62, -47.21) * mm, "end": v(-31.96, -46.96) * mm});
            skLineSegment(sketch, "E782", {"start": v(-31.96, -46.96) * mm, "end": v(-31.34, -46.7) * mm});
            skLineSegment(sketch, "E783", {"start": v(-31.34, -46.7) * mm, "end": v(-30.73, -46.43) * mm});
            skLineSegment(sketch, "E784", {"start": v(-30.73, -46.43) * mm, "end": v(-30.16, -46.16) * mm});
            skLineSegment(sketch, "E785", {"start": v(-30.16, -46.16) * mm, "end": v(-29.6, -45.9) * mm});
            skLineSegment(sketch, "E786", {"start": v(-29.6, -45.9) * mm, "end": v(-29.09, -45.62) * mm});
            skLineSegment(sketch, "E787", {"start": v(-29.09, -45.62) * mm, "end": v(-28.59, -45.35) * mm});
            skLineSegment(sketch, "E788", {"start": v(-28.59, -45.35) * mm, "end": v(-28.12, -45.08) * mm});
            skLineSegment(sketch, "E789", {"start": v(-28.12, -45.08) * mm, "end": v(-27.67, -44.8) * mm});
            skLineSegment(sketch, "E790", {"start": v(-27.67, -44.8) * mm, "end": v(-27.25, -44.54) * mm});
            skLineSegment(sketch, "E791", {"start": v(-27.25, -44.54) * mm, "end": v(-26.85, -44.27) * mm});
            skLineSegment(sketch, "E792", {"start": v(-26.85, -44.27) * mm, "end": v(-26.48, -44.01) * mm});
            skLineSegment(sketch, "E793", {"start": v(-26.48, -44.01) * mm, "end": v(-26.13, -43.75) * mm});
            skLineSegment(sketch, "E794", {"start": v(-26.13, -43.75) * mm, "end": v(-25.8, -43.5) * mm});
            skLineSegment(sketch, "E795", {"start": v(-25.8, -43.5) * mm, "end": v(-25.5, -43.26) * mm});
            skLineSegment(sketch, "E796", {"start": v(-25.5, -43.26) * mm, "end": v(-25.22, -43.03) * mm});
            skLineSegment(sketch, "E797", {"start": v(-25.22, -43.03) * mm, "end": v(-24.96, -42.8) * mm});
            skLineSegment(sketch, "E798", {"start": v(-24.96, -42.8) * mm, "end": v(-24.72, -42.58) * mm});
            skLineSegment(sketch, "E799", {"start": v(-24.72, -42.58) * mm, "end": v(-24.5, -42.38) * mm});
            skLineSegment(sketch, "E800", {"start": v(-24.5, -42.38) * mm, "end": v(-24.31, -42.18) * mm});
            skLineSegment(sketch, "E801", {"start": v(-24.31, -42.18) * mm, "end": v(-24.14, -42) * mm});
            skLineSegment(sketch, "E802", {"start": v(-24.14, -42) * mm, "end": v(-23.98, -41.83) * mm});
            skLineSegment(sketch, "E803", {"start": v(-23.98, -41.83) * mm, "end": v(-23.84, -41.67) * mm});
            skLineSegment(sketch, "E804", {"start": v(-23.84, -41.67) * mm, "end": v(-23.72, -41.53) * mm});
            skLineSegment(sketch, "E805", {"start": v(-23.72, -41.53) * mm, "end": v(-23.62, -41.4) * mm});
            skLineSegment(sketch, "E806", {"start": v(-23.62, -41.4) * mm, "end": v(-23.53, -41.29) * mm});
            skLineSegment(sketch, "E807", {"start": v(-23.53, -41.29) * mm, "end": v(-23.46, -41.2) * mm});
            skLineSegment(sketch, "E808", {"start": v(-23.46, -41.2) * mm, "end": v(-23.4, -41.12) * mm});
            skLineSegment(sketch, "E809", {"start": v(-23.4, -41.12) * mm, "end": v(-23.37, -41.05) * mm});
            skLineSegment(sketch, "E810", {"start": v(-23.37, -41.05) * mm, "end": v(-23.34, -41) * mm});
            skLineSegment(sketch, "E811", {"start": v(-23.34, -41) * mm, "end": v(-23.32, -40.98) * mm});
            skLineSegment(sketch, "E812", {"start": v(-23.32, -40.98) * mm, "end": v(-22.4, -39.38) * mm});
            skLineSegment(sketch, "E813", {"start": v(-22.4, -39.38) * mm, "end": v(-17.34, -41.86) * mm});
            skLineSegment(sketch, "E814", {"start": v(-17.34, -41.86) * mm, "end": v(-18.05, -43.57) * mm});
            skLineSegment(sketch, "E815", {"start": v(-18.05, -43.57) * mm, "end": v(-18.06, -43.6) * mm});
            skLineSegment(sketch, "E816", {"start": v(-18.06, -43.6) * mm, "end": v(-18.07, -43.64) * mm});
            skLineSegment(sketch, "E817", {"start": v(-18.07, -43.64) * mm, "end": v(-18.1, -43.71) * mm});
            skLineSegment(sketch, "E818", {"start": v(-18.1, -43.71) * mm, "end": v(-18.13, -43.8) * mm});
            skLineSegment(sketch, "E819", {"start": v(-18.13, -43.8) * mm, "end": v(-18.16, -43.92) * mm});
            skLineSegment(sketch, "E820", {"start": v(-18.16, -43.92) * mm, "end": v(-18.2, -44.06) * mm});
            skLineSegment(sketch, "E821", {"start": v(-18.2, -44.06) * mm, "end": v(-18.23, -44.22) * mm});
            skLineSegment(sketch, "E822", {"start": v(-18.23, -44.22) * mm, "end": v(-18.27, -44.4) * mm});
            skLineSegment(sketch, "E823", {"start": v(-18.27, -44.4) * mm, "end": v(-18.3, -44.6) * mm});
            skLineSegment(sketch, "E824", {"start": v(-18.3, -44.6) * mm, "end": v(-18.35, -44.83) * mm});
            skLineSegment(sketch, "E825", {"start": v(-18.35, -44.83) * mm, "end": v(-18.39, -45.08) * mm});
            skLineSegment(sketch, "E826", {"start": v(-18.39, -45.08) * mm, "end": v(-18.42, -45.36) * mm});
            skLineSegment(sketch, "E827", {"start": v(-18.42, -45.36) * mm, "end": v(-18.45, -45.65) * mm});
            skLineSegment(sketch, "E828", {"start": v(-18.45, -45.65) * mm, "end": v(-18.48, -45.97) * mm});
            skLineSegment(sketch, "E829", {"start": v(-18.48, -45.97) * mm, "end": v(-18.5, -46.31) * mm});
            skLineSegment(sketch, "E830", {"start": v(-18.5, -46.31) * mm, "end": v(-18.5, -46.68) * mm});
            skLineSegment(sketch, "E831", {"start": v(-18.5, -46.68) * mm, "end": v(-18.52, -47.07) * mm});
            skLineSegment(sketch, "E832", {"start": v(-18.52, -47.07) * mm, "end": v(-18.51, -47.48) * mm});
            skLineSegment(sketch, "E833", {"start": v(-18.51, -47.48) * mm, "end": v(-18.5, -47.91) * mm});
            skLineSegment(sketch, "E834", {"start": v(-18.5, -47.91) * mm, "end": v(-18.48, -48.37) * mm});
            skLineSegment(sketch, "E835", {"start": v(-18.48, -48.37) * mm, "end": v(-18.44, -48.84) * mm});
            skLineSegment(sketch, "E836", {"start": v(-18.44, -48.84) * mm, "end": v(-18.4, -49.34) * mm});
            skLineSegment(sketch, "E837", {"start": v(-18.4, -49.34) * mm, "end": v(-18.34, -49.86) * mm});
            skLineSegment(sketch, "E838", {"start": v(-18.34, -49.86) * mm, "end": v(-18.26, -50.4) * mm});
            skLineSegment(sketch, "E839", {"start": v(-18.26, -50.4) * mm, "end": v(-18.17, -50.96) * mm});
            skLineSegment(sketch, "E840", {"start": v(-18.17, -50.96) * mm, "end": v(-18.06, -51.54) * mm});
            skLineSegment(sketch, "E841", {"start": v(-18.06, -51.54) * mm, "end": v(-17.94, -52.14) * mm});
            skLineSegment(sketch, "E842", {"start": v(-17.94, -52.14) * mm, "end": v(-17.8, -52.76) * mm});
            skLineSegment(sketch, "E843", {"start": v(-17.8, -52.76) * mm, "end": v(-17.64, -53.4) * mm});
            skLineSegment(sketch, "E844", {"start": v(-17.64, -53.4) * mm, "end": v(-17.46, -54.05) * mm});
            skLineSegment(sketch, "E845", {"start": v(-17.46, -54.05) * mm, "end": v(-17.26, -54.73) * mm});
            skLineSegment(sketch, "E846", {"start": v(-17.26, -54.73) * mm, "end": v(-17.04, -55.42) * mm});
            skLineSegment(sketch, "E847", {"start": v(-17.04, -55.42) * mm, "end": v(-16.8, -56.12) * mm});
            skLineSegment(sketch, "E848", {"start": v(-16.8, -56.12) * mm, "end": v(-16.52, -56.85) * mm});
            skLineSegment(sketch, "E849", {"start": v(-16.52, -56.85) * mm, "end": v(-16.15, -57.3) * mm});
            skLineSegment(sketch, "E850", {"start": v(-16.15, -57.3) * mm, "end": v(-14.3, -57.79) * mm});
            skLineSegment(sketch, "E851", {"start": v(-14.3, -57.79) * mm, "end": v(-13.76, -57.58) * mm});
            skLineSegment(sketch, "E852", {"start": v(-13.76, -57.58) * mm, "end": v(-13.17, -57.08) * mm});
            skLineSegment(sketch, "E853", {"start": v(-13.17, -57.08) * mm, "end": v(-12.6, -56.6) * mm});
            skLineSegment(sketch, "E854", {"start": v(-12.6, -56.6) * mm, "end": v(-12.07, -56.1) * mm});
            skLineSegment(sketch, "E855", {"start": v(-12.07, -56.1) * mm, "end": v(-11.56, -55.62) * mm});
            skLineSegment(sketch, "E856", {"start": v(-11.56, -55.62) * mm, "end": v(-11.08, -55.14) * mm});
            skLineSegment(sketch, "E857", {"start": v(-11.08, -55.14) * mm, "end": v(-10.63, -54.66) * mm});
            skLineSegment(sketch, "E858", {"start": v(-10.63, -54.66) * mm, "end": v(-10.2, -54.2) * mm});
            skLineSegment(sketch, "E859", {"start": v(-10.2, -54.2) * mm, "end": v(-9.8, -53.73) * mm});
            skLineSegment(sketch, "E860", {"start": v(-9.8, -53.73) * mm, "end": v(-9.41, -53.28) * mm});
            skLineSegment(sketch, "E861", {"start": v(-9.41, -53.28) * mm, "end": v(-9.06, -52.84) * mm});
            skLineSegment(sketch, "E862", {"start": v(-9.06, -52.84) * mm, "end": v(-8.73, -52.4) * mm});
            skLineSegment(sketch, "E863", {"start": v(-8.73, -52.4) * mm, "end": v(-8.42, -51.98) * mm});
            skLineSegment(sketch, "E864", {"start": v(-8.42, -51.98) * mm, "end": v(-8.13, -51.57) * mm});
            skLineSegment(sketch, "E865", {"start": v(-8.13, -51.57) * mm, "end": v(-7.86, -51.18) * mm});
            skLineSegment(sketch, "E866", {"start": v(-7.86, -51.18) * mm, "end": v(-7.62, -50.8) * mm});
            skLineSegment(sketch, "E867", {"start": v(-7.62, -50.8) * mm, "end": v(-7.4, -50.42) * mm});
            skLineSegment(sketch, "E868", {"start": v(-7.4, -50.42) * mm, "end": v(-7.19, -50.07) * mm});
            skLineSegment(sketch, "E869", {"start": v(-7.19, -50.07) * mm, "end": v(-7, -49.73) * mm});
            skLineSegment(sketch, "E870", {"start": v(-7, -49.73) * mm, "end": v(-6.83, -49.4) * mm});
            skLineSegment(sketch, "E871", {"start": v(-6.83, -49.4) * mm, "end": v(-6.68, -49.1) * mm});
            skLineSegment(sketch, "E872", {"start": v(-6.68, -49.1) * mm, "end": v(-6.54, -48.8) * mm});
            skLineSegment(sketch, "E873", {"start": v(-6.54, -48.8) * mm, "end": v(-6.42, -48.53) * mm});
            skLineSegment(sketch, "E874", {"start": v(-6.42, -48.53) * mm, "end": v(-6.32, -48.27) * mm});
            skLineSegment(sketch, "E875", {"start": v(-6.32, -48.27) * mm, "end": v(-6.23, -48.04) * mm});
            skLineSegment(sketch, "E876", {"start": v(-6.23, -48.04) * mm, "end": v(-6.15, -47.82) * mm});
            skLineSegment(sketch, "E877", {"start": v(-6.15, -47.82) * mm, "end": v(-6.08, -47.62) * mm});
            skLineSegment(sketch, "E878", {"start": v(-6.08, -47.62) * mm, "end": v(-6.02, -47.45) * mm});
            skLineSegment(sketch, "E879", {"start": v(-6.02, -47.45) * mm, "end": v(-5.98, -47.29) * mm});
            skLineSegment(sketch, "E880", {"start": v(-5.98, -47.29) * mm, "end": v(-5.94, -47.15) * mm});
            skLineSegment(sketch, "E881", {"start": v(-5.94, -47.15) * mm, "end": v(-5.91, -47.04) * mm});
            skLineSegment(sketch, "E882", {"start": v(-5.91, -47.04) * mm, "end": v(-5.9, -46.94) * mm});
            skLineSegment(sketch, "E883", {"start": v(-5.9, -46.94) * mm, "end": v(-5.88, -46.87) * mm});
            skLineSegment(sketch, "E884", {"start": v(-5.88, -46.87) * mm, "end": v(-5.87, -46.82) * mm});
            skLineSegment(sketch, "E885", {"start": v(-5.87, -46.82) * mm, "end": v(-5.86, -46.79) * mm});
            skLineSegment(sketch, "E886", {"start": v(-5.86, -46.79) * mm, "end": v(-5.63, -44.96) * mm});
            skLineSegment(sketch, "E887", {"start": v(-5.63, -44.96) * mm, "end": v(0, -45.3) * mm});
            skLineSegment(sketch, "E888", {"start": v(0, -45.3) * mm, "end": v(0, -47.16) * mm});
            skLineSegment(sketch, "E889", {"start": v(0, -47.16) * mm, "end": v(0, -47.19) * mm});
            skLineSegment(sketch, "E890", {"start": v(0, -47.19) * mm, "end": v(0, -47.24) * mm});
            skLineSegment(sketch, "E891", {"start": v(0, -47.24) * mm, "end": v(0, -47.31) * mm});
            skLineSegment(sketch, "E892", {"start": v(0, -47.31) * mm, "end": v(0.02, -47.4) * mm});
            skLineSegment(sketch, "E893", {"start": v(0.02, -47.4) * mm, "end": v(0.03, -47.52) * mm});
            skLineSegment(sketch, "E894", {"start": v(0.03, -47.52) * mm, "end": v(0.05, -47.66) * mm});
            skLineSegment(sketch, "E895", {"start": v(0.05, -47.66) * mm, "end": v(0.08, -47.83) * mm});
            skLineSegment(sketch, "E896", {"start": v(0.08, -47.83) * mm, "end": v(0.11, -48) * mm});
            skLineSegment(sketch, "E897", {"start": v(0.11, -48) * mm, "end": v(0.15, -48.21) * mm});
            skLineSegment(sketch, "E898", {"start": v(0.15, -48.21) * mm, "end": v(0.2, -48.44) * mm});
            skLineSegment(sketch, "E899", {"start": v(0.2, -48.44) * mm, "end": v(0.27, -48.69) * mm});
            skLineSegment(sketch, "E900", {"start": v(0.27, -48.69) * mm, "end": v(0.34, -48.95) * mm});
            skLineSegment(sketch, "E901", {"start": v(0.34, -48.95) * mm, "end": v(0.42, -49.24) * mm});
            skLineSegment(sketch, "E902", {"start": v(0.42, -49.24) * mm, "end": v(0.52, -49.54) * mm});
            skLineSegment(sketch, "E903", {"start": v(0.52, -49.54) * mm, "end": v(0.64, -49.87) * mm});
            skLineSegment(sketch, "E904", {"start": v(0.64, -49.87) * mm, "end": v(0.76, -50.21) * mm});
            skLineSegment(sketch, "E905", {"start": v(0.76, -50.21) * mm, "end": v(0.9, -50.57) * mm});
            skLineSegment(sketch, "E906", {"start": v(0.9, -50.57) * mm, "end": v(1.07, -50.95) * mm});
            skLineSegment(sketch, "E907", {"start": v(1.07, -50.95) * mm, "end": v(1.24, -51.34) * mm});
            skLineSegment(sketch, "E908", {"start": v(1.24, -51.34) * mm, "end": v(1.44, -51.76) * mm});
            skLineSegment(sketch, "E909", {"start": v(1.44, -51.76) * mm, "end": v(1.65, -52.18) * mm});
            skLineSegment(sketch, "E910", {"start": v(1.65, -52.18) * mm, "end": v(1.89, -52.63) * mm});
            skLineSegment(sketch, "E911", {"start": v(1.89, -52.63) * mm, "end": v(2.14, -53.08) * mm});
            skLineSegment(sketch, "E912", {"start": v(2.14, -53.08) * mm, "end": v(2.42, -53.55) * mm});
            skLineSegment(sketch, "E913", {"start": v(2.42, -53.55) * mm, "end": v(2.71, -54.04) * mm});
            skLineSegment(sketch, "E914", {"start": v(2.71, -54.04) * mm, "end": v(3.04, -54.53) * mm});
            skLineSegment(sketch, "E915", {"start": v(3.04, -54.53) * mm, "end": v(3.38, -55.04) * mm});
            skLineSegment(sketch, "E916", {"start": v(3.38, -55.04) * mm, "end": v(3.75, -55.56) * mm});
            skLineSegment(sketch, "E917", {"start": v(3.75, -55.56) * mm, "end": v(4.14, -56.08) * mm});
            skLineSegment(sketch, "E918", {"start": v(4.14, -56.08) * mm, "end": v(4.56, -56.62) * mm});
            skLineSegment(sketch, "E919", {"start": v(4.56, -56.62) * mm, "end": v(5, -57.17) * mm});
            skLineSegment(sketch, "E920", {"start": v(5, -57.17) * mm, "end": v(5.47, -57.72) * mm});
            skLineSegment(sketch, "E921", {"start": v(5.47, -57.72) * mm, "end": v(5.97, -58.28) * mm});
            skLineSegment(sketch, "E922", {"start": v(5.97, -58.28) * mm, "end": v(6.49, -58.84) * mm});
            skLineSegment(sketch, "E923", {"start": v(6.49, -58.84) * mm, "end": v(7, -59.12) * mm});
            skLineSegment(sketch, "E924", {"start": v(7, -59.12) * mm, "end": v(8.9, -58.86) * mm});
            skLineSegment(sketch, "E925", {"start": v(8.9, -58.86) * mm, "end": v(9.33, -58.46) * mm});
            skLineSegment(sketch, "E926", {"start": v(9.33, -58.46) * mm, "end": v(9.68, -57.78) * mm});
            skLineSegment(sketch, "E927", {"start": v(9.68, -57.78) * mm, "end": v(10.01, -57.1) * mm});
            skLineSegment(sketch, "E928", {"start": v(10.01, -57.1) * mm, "end": v(10.32, -56.45) * mm});
            skLineSegment(sketch, "E929", {"start": v(10.32, -56.45) * mm, "end": v(10.6, -55.8) * mm});
            skLineSegment(sketch, "E930", {"start": v(10.6, -55.8) * mm, "end": v(10.86, -55.18) * mm});
            skLineSegment(sketch, "E931", {"start": v(10.86, -55.18) * mm, "end": v(11.1, -54.57) * mm});
            skLineSegment(sketch, "E932", {"start": v(11.1, -54.57) * mm, "end": v(11.32, -53.97) * mm});
            skLineSegment(sketch, "E933", {"start": v(11.32, -53.97) * mm, "end": v(11.52, -53.39) * mm});
            skLineSegment(sketch, "E934", {"start": v(11.52, -53.39) * mm, "end": v(11.7, -52.83) * mm});
            skLineSegment(sketch, "E935", {"start": v(11.7, -52.83) * mm, "end": v(11.85, -52.28) * mm});
            skLineSegment(sketch, "E936", {"start": v(11.85, -52.28) * mm, "end": v(12, -51.75) * mm});
            skLineSegment(sketch, "E937", {"start": v(12, -51.75) * mm, "end": v(12.12, -51.25) * mm});
            skLineSegment(sketch, "E938", {"start": v(12.12, -51.25) * mm, "end": v(12.23, -50.76) * mm});
            skLineSegment(sketch, "E939", {"start": v(12.23, -50.76) * mm, "end": v(12.32, -50.3) * mm});
            skLineSegment(sketch, "E940", {"start": v(12.32, -50.3) * mm, "end": v(12.4, -49.84) * mm});
            skLineSegment(sketch, "E941", {"start": v(12.4, -49.84) * mm, "end": v(12.46, -49.41) * mm});
            skLineSegment(sketch, "E942", {"start": v(12.46, -49.41) * mm, "end": v(12.52, -49) * mm});
            skLineSegment(sketch, "E943", {"start": v(12.52, -49) * mm, "end": v(12.56, -48.62) * mm});
            skLineSegment(sketch, "E944", {"start": v(12.56, -48.62) * mm, "end": v(12.6, -48.26) * mm});
            skLineSegment(sketch, "E945", {"start": v(12.6, -48.26) * mm, "end": v(12.62, -47.91) * mm});
            skLineSegment(sketch, "E946", {"start": v(12.62, -47.91) * mm, "end": v(12.63, -47.6) * mm});
            skLineSegment(sketch, "E947", {"start": v(12.63, -47.6) * mm, "end": v(12.64, -47.3) * mm});
            skLineSegment(sketch, "E948", {"start": v(12.64, -47.3) * mm, "end": v(12.64, -47.02) * mm});
            skLineSegment(sketch, "E949", {"start": v(12.64, -47.02) * mm, "end": v(12.63, -46.76) * mm});
            skLineSegment(sketch, "E950", {"start": v(12.63, -46.76) * mm, "end": v(12.62, -46.53) * mm});
            skLineSegment(sketch, "E951", {"start": v(12.62, -46.53) * mm, "end": v(12.6, -46.33) * mm});
            skLineSegment(sketch, "E952", {"start": v(12.6, -46.33) * mm, "end": v(12.6, -46.14) * mm});
            skLineSegment(sketch, "E953", {"start": v(12.6, -46.14) * mm, "end": v(12.57, -45.98) * mm});
            skLineSegment(sketch, "E954", {"start": v(12.57, -45.98) * mm, "end": v(12.56, -45.84) * mm});
            skLineSegment(sketch, "E955", {"start": v(12.56, -45.84) * mm, "end": v(12.54, -45.72) * mm});
            skLineSegment(sketch, "E956", {"start": v(12.54, -45.72) * mm, "end": v(12.52, -45.62) * mm});
            skLineSegment(sketch, "E957", {"start": v(12.52, -45.62) * mm, "end": v(12.5, -45.55) * mm});
            skLineSegment(sketch, "E958", {"start": v(12.5, -45.55) * mm, "end": v(12.5, -45.5) * mm});
            skLineSegment(sketch, "E959", {"start": v(12.5, -45.5) * mm, "end": v(12.49, -45.47) * mm});
            skLineSegment(sketch, "E960", {"start": v(12.49, -45.47) * mm, "end": v(12, -43.7) * mm});
            skLineSegment(sketch, "E961", {"start": v(12, -43.7) * mm, "end": v(17.34, -41.86) * mm});
            skLineSegment(sketch, "E962", {"start": v(17.34, -41.86) * mm, "end": v(18.05, -43.57) * mm});
            skLineSegment(sketch, "E963", {"start": v(18.05, -43.57) * mm, "end": v(18.06, -43.6) * mm});
            skLineSegment(sketch, "E964", {"start": v(18.06, -43.6) * mm, "end": v(18.08, -43.64) * mm});
            skLineSegment(sketch, "E965", {"start": v(18.08, -43.64) * mm, "end": v(18.11, -43.7) * mm});
            skLineSegment(sketch, "E966", {"start": v(18.11, -43.7) * mm, "end": v(18.16, -43.8) * mm});
            skLineSegment(sketch, "E967", {"start": v(18.16, -43.8) * mm, "end": v(18.22, -43.9) * mm});
            skLineSegment(sketch, "E968", {"start": v(18.22, -43.9) * mm, "end": v(18.29, -44.02) * mm});
            skLineSegment(sketch, "E969", {"start": v(18.29, -44.02) * mm, "end": v(18.37, -44.16) * mm});
            skLineSegment(sketch, "E970", {"start": v(18.37, -44.16) * mm, "end": v(18.48, -44.31) * mm});
            skLineSegment(sketch, "E971", {"start": v(18.48, -44.31) * mm, "end": v(18.6, -44.49) * mm});
            skLineSegment(sketch, "E972", {"start": v(18.6, -44.49) * mm, "end": v(18.73, -44.67) * mm});
            skLineSegment(sketch, "E973", {"start": v(18.73, -44.67) * mm, "end": v(18.88, -44.88) * mm});
            skLineSegment(sketch, "E974", {"start": v(18.88, -44.88) * mm, "end": v(19.05, -45.1) * mm});
            skLineSegment(sketch, "E975", {"start": v(19.05, -45.1) * mm, "end": v(19.23, -45.33) * mm});
            skLineSegment(sketch, "E976", {"start": v(19.23, -45.33) * mm, "end": v(19.44, -45.57) * mm});
            skLineSegment(sketch, "E977", {"start": v(19.44, -45.57) * mm, "end": v(19.67, -45.83) * mm});
            skLineSegment(sketch, "E978", {"start": v(19.67, -45.83) * mm, "end": v(19.92, -46.1) * mm});
            skLineSegment(sketch, "E979", {"start": v(19.92, -46.1) * mm, "end": v(20.2, -46.38) * mm});
            skLineSegment(sketch, "E980", {"start": v(20.2, -46.38) * mm, "end": v(20.48, -46.66) * mm});
            skLineSegment(sketch, "E981", {"start": v(20.48, -46.66) * mm, "end": v(20.8, -46.96) * mm});
            skLineSegment(sketch, "E982", {"start": v(20.8, -46.96) * mm, "end": v(21.13, -47.27) * mm});
            skLineSegment(sketch, "E983", {"start": v(21.13, -47.27) * mm, "end": v(21.5, -47.58) * mm});
            skLineSegment(sketch, "E984", {"start": v(21.5, -47.58) * mm, "end": v(21.88, -47.9) * mm});
            skLineSegment(sketch, "E985", {"start": v(21.88, -47.9) * mm, "end": v(22.3, -48.22) * mm});
            skLineSegment(sketch, "E986", {"start": v(22.3, -48.22) * mm, "end": v(22.73, -48.55) * mm});
            skLineSegment(sketch, "E987", {"start": v(22.73, -48.55) * mm, "end": v(23.19, -48.88) * mm});
            skLineSegment(sketch, "E988", {"start": v(23.19, -48.88) * mm, "end": v(23.67, -49.22) * mm});
            skLineSegment(sketch, "E989", {"start": v(23.67, -49.22) * mm, "end": v(24.18, -49.56) * mm});
            skLineSegment(sketch, "E990", {"start": v(24.18, -49.56) * mm, "end": v(24.72, -49.9) * mm});
            skLineSegment(sketch, "E991", {"start": v(24.72, -49.9) * mm, "end": v(25.29, -50.23) * mm});
            skLineSegment(sketch, "E992", {"start": v(25.29, -50.23) * mm, "end": v(25.88, -50.57) * mm});
            skLineSegment(sketch, "E993", {"start": v(25.88, -50.57) * mm, "end": v(26.5, -50.9) * mm});
            skLineSegment(sketch, "E994", {"start": v(26.5, -50.9) * mm, "end": v(27.14, -51.23) * mm});
            skLineSegment(sketch, "E995", {"start": v(27.14, -51.23) * mm, "end": v(27.81, -51.56) * mm});
            skLineSegment(sketch, "E996", {"start": v(27.81, -51.56) * mm, "end": v(28.51, -51.88) * mm});
            skLineSegment(sketch, "E997", {"start": v(28.51, -51.88) * mm, "end": v(29.1, -51.94) * mm});
            skLineSegment(sketch, "E998", {"start": v(29.1, -51.94) * mm, "end": v(30.75, -50.98) * mm});
            skLineSegment(sketch, "E999", {"start": v(30.75, -50.98) * mm, "end": v(30.99, -50.44) * mm});
            skLineSegment(sketch, "E1000", {"start": v(30.99, -50.44) * mm, "end": v(31.05, -49.67) * mm});
            skLineSegment(sketch, "E1001", {"start": v(31.05, -49.67) * mm, "end": v(31.1, -48.93) * mm});
            skLineSegment(sketch, "E1002", {"start": v(31.1, -48.93) * mm, "end": v(31.14, -48.2) * mm});
            skLineSegment(sketch, "E1003", {"start": v(31.14, -48.2) * mm, "end": v(31.15, -47.5) * mm});
            skLineSegment(sketch, "E1004", {"start": v(31.15, -47.5) * mm, "end": v(31.15, -46.82) * mm});
            skLineSegment(sketch, "E1005", {"start": v(31.15, -46.82) * mm, "end": v(31.14, -46.16) * mm});
            skLineSegment(sketch, "E1006", {"start": v(31.14, -46.16) * mm, "end": v(31.1, -45.53) * mm});
            skLineSegment(sketch, "E1007", {"start": v(31.1, -45.53) * mm, "end": v(31.07, -44.92) * mm});
            skLineSegment(sketch, "E1008", {"start": v(31.07, -44.92) * mm, "end": v(31.02, -44.33) * mm});
            skLineSegment(sketch, "E1009", {"start": v(31.02, -44.33) * mm, "end": v(30.96, -43.77) * mm});
            skLineSegment(sketch, "E1010", {"start": v(30.96, -43.77) * mm, "end": v(30.89, -43.23) * mm});
            skLineSegment(sketch, "E1011", {"start": v(30.89, -43.23) * mm, "end": v(30.8, -42.7) * mm});
            skLineSegment(sketch, "E1012", {"start": v(30.8, -42.7) * mm, "end": v(30.72, -42.22) * mm});
            skLineSegment(sketch, "E1013", {"start": v(30.72, -42.22) * mm, "end": v(30.63, -41.75) * mm});
            skLineSegment(sketch, "E1014", {"start": v(30.63, -41.75) * mm, "end": v(30.53, -41.3) * mm});
            skLineSegment(sketch, "E1015", {"start": v(30.53, -41.3) * mm, "end": v(30.43, -40.88) * mm});
            skLineSegment(sketch, "E1016", {"start": v(30.43, -40.88) * mm, "end": v(30.32, -40.49) * mm});
            skLineSegment(sketch, "E1017", {"start": v(30.32, -40.49) * mm, "end": v(30.21, -40.11) * mm});
            skLineSegment(sketch, "E1018", {"start": v(30.21, -40.11) * mm, "end": v(30.1, -39.76) * mm});
            skLineSegment(sketch, "E1019", {"start": v(30.1, -39.76) * mm, "end": v(30, -39.44) * mm});
            skLineSegment(sketch, "E1020", {"start": v(30, -39.44) * mm, "end": v(29.88, -39.14) * mm});
            skLineSegment(sketch, "E1021", {"start": v(29.88, -39.14) * mm, "end": v(29.77, -38.86) * mm});
            skLineSegment(sketch, "E1022", {"start": v(29.77, -38.86) * mm, "end": v(29.67, -38.6) * mm});
            skLineSegment(sketch, "E1023", {"start": v(29.67, -38.6) * mm, "end": v(29.57, -38.37) * mm});
            skLineSegment(sketch, "E1024", {"start": v(29.57, -38.37) * mm, "end": v(29.47, -38.16) * mm});
            skLineSegment(sketch, "E1025", {"start": v(29.47, -38.16) * mm, "end": v(29.38, -37.97) * mm});
            skLineSegment(sketch, "E1026", {"start": v(29.38, -37.97) * mm, "end": v(29.3, -37.8) * mm});
            skLineSegment(sketch, "E1027", {"start": v(29.3, -37.8) * mm, "end": v(29.21, -37.67) * mm});
            skLineSegment(sketch, "E1028", {"start": v(29.21, -37.67) * mm, "end": v(29.14, -37.54) * mm});
            skLineSegment(sketch, "E1029", {"start": v(29.14, -37.54) * mm, "end": v(29.08, -37.44) * mm});
            skLineSegment(sketch, "E1030", {"start": v(29.08, -37.44) * mm, "end": v(29.03, -37.36) * mm});
            skLineSegment(sketch, "E1031", {"start": v(29.03, -37.36) * mm, "end": v(28.99, -37.3) * mm});
            skLineSegment(sketch, "E1032", {"start": v(28.99, -37.3) * mm, "end": v(28.96, -37.26) * mm});
            skLineSegment(sketch, "E1033", {"start": v(28.96, -37.26) * mm, "end": v(28.94, -37.23) * mm});
            skLineSegment(sketch, "E1034", {"start": v(28.94, -37.23) * mm, "end": v(27.8, -35.77) * mm});
            skLineSegment(sketch, "E1035", {"start": v(27.8, -35.77) * mm, "end": v(32.04, -32.04) * mm});
            skLineSegment(sketch, "E1036", {"start": v(32.04, -32.04) * mm, "end": v(33.34, -33.34) * mm});
            skLineSegment(sketch, "E1037", {"start": v(33.34, -33.34) * mm, "end": v(33.37, -33.36) * mm});
            skLineSegment(sketch, "E1038", {"start": v(33.37, -33.36) * mm, "end": v(33.4, -33.4) * mm});
            skLineSegment(sketch, "E1039", {"start": v(33.4, -33.4) * mm, "end": v(33.46, -33.45) * mm});
            skLineSegment(sketch, "E1040", {"start": v(33.46, -33.45) * mm, "end": v(33.53, -33.5) * mm});
            skLineSegment(sketch, "E1041", {"start": v(33.53, -33.5) * mm, "end": v(33.63, -33.58) * mm});
            skLineSegment(sketch, "E1042", {"start": v(33.63, -33.58) * mm, "end": v(33.74, -33.67) * mm});
            skLineSegment(sketch, "E1043", {"start": v(33.74, -33.67) * mm, "end": v(33.87, -33.76) * mm});
            skLineSegment(sketch, "E1044", {"start": v(33.87, -33.76) * mm, "end": v(34.03, -33.87) * mm});
            skLineSegment(sketch, "E1045", {"start": v(34.03, -33.87) * mm, "end": v(34.2, -33.99) * mm});
            skLineSegment(sketch, "E1046", {"start": v(34.2, -33.99) * mm, "end": v(34.4, -34.1) * mm});
            skLineSegment(sketch, "E1047", {"start": v(34.4, -34.1) * mm, "end": v(34.61, -34.24) * mm});
            skLineSegment(sketch, "E1048", {"start": v(34.61, -34.24) * mm, "end": v(34.85, -34.37) * mm});
            skLineSegment(sketch, "E1049", {"start": v(34.85, -34.37) * mm, "end": v(35.12, -34.52) * mm});
            skLineSegment(sketch, "E1050", {"start": v(35.12, -34.52) * mm, "end": v(35.4, -34.66) * mm});
            skLineSegment(sketch, "E1051", {"start": v(35.4, -34.66) * mm, "end": v(35.71, -34.81) * mm});
            skLineSegment(sketch, "E1052", {"start": v(35.71, -34.81) * mm, "end": v(36.04, -34.96) * mm});
            skLineSegment(sketch, "E1053", {"start": v(36.04, -34.96) * mm, "end": v(36.4, -35.12) * mm});
            skLineSegment(sketch, "E1054", {"start": v(36.4, -35.12) * mm, "end": v(36.78, -35.27) * mm});
            skLineSegment(sketch, "E1055", {"start": v(36.78, -35.27) * mm, "end": v(37.18, -35.43) * mm});
            skLineSegment(sketch, "E1056", {"start": v(37.18, -35.43) * mm, "end": v(37.61, -35.58) * mm});
            skLineSegment(sketch, "E1057", {"start": v(37.61, -35.58) * mm, "end": v(38.07, -35.73) * mm});
            skLineSegment(sketch, "E1058", {"start": v(38.07, -35.73) * mm, "end": v(38.55, -35.88) * mm});
            skLineSegment(sketch, "E1059", {"start": v(38.55, -35.88) * mm, "end": v(39.05, -36.02) * mm});
            skLineSegment(sketch, "E1060", {"start": v(39.05, -36.02) * mm, "end": v(39.58, -36.16) * mm});
            skLineSegment(sketch, "E1061", {"start": v(39.58, -36.16) * mm, "end": v(40.13, -36.3) * mm});
            skLineSegment(sketch, "E1062", {"start": v(40.13, -36.3) * mm, "end": v(40.7, -36.41) * mm});
            skLineSegment(sketch, "E1063", {"start": v(40.7, -36.41) * mm, "end": v(41.3, -36.53) * mm});
            skLineSegment(sketch, "E1064", {"start": v(41.3, -36.53) * mm, "end": v(41.93, -36.64) * mm});
            skLineSegment(sketch, "E1065", {"start": v(41.93, -36.64) * mm, "end": v(42.58, -36.73) * mm});
            skLineSegment(sketch, "E1066", {"start": v(42.58, -36.73) * mm, "end": v(43.26, -36.82) * mm});
            skLineSegment(sketch, "E1067", {"start": v(43.26, -36.82) * mm, "end": v(43.96, -36.89) * mm});
            skLineSegment(sketch, "E1068", {"start": v(43.96, -36.89) * mm, "end": v(44.68, -36.95) * mm});
            skLineSegment(sketch, "E1069", {"start": v(44.68, -36.95) * mm, "end": v(45.43, -36.99) * mm});
            skLineSegment(sketch, "E1070", {"start": v(45.43, -36.99) * mm, "end": v(46.2, -37.02) * mm});
            skLineSegment(sketch, "E1071", {"start": v(46.2, -37.02) * mm, "end": v(46.76, -36.85) * mm});
            skLineSegment(sketch, "E1072", {"start": v(46.76, -36.85) * mm, "end": v(47.91, -35.33) * mm});
            skLineSegment(sketch, "E1073", {"start": v(47.91, -35.33) * mm, "end": v(47.93, -34.74) * mm});
            skLineSegment(sketch, "E1074", {"start": v(47.93, -34.74) * mm, "end": v(47.7, -34) * mm});
            skLineSegment(sketch, "E1075", {"start": v(47.7, -34) * mm, "end": v(47.46, -33.3) * mm});
            skLineSegment(sketch, "E1076", {"start": v(47.46, -33.3) * mm, "end": v(47.21, -32.62) * mm});
            skLineSegment(sketch, "E1077", {"start": v(47.21, -32.62) * mm, "end": v(46.96, -31.96) * mm});
            skLineSegment(sketch, "E1078", {"start": v(46.96, -31.96) * mm, "end": v(46.7, -31.34) * mm});
            skLineSegment(sketch, "E1079", {"start": v(46.7, -31.34) * mm, "end": v(46.43, -30.73) * mm});
            skLineSegment(sketch, "E1080", {"start": v(46.43, -30.73) * mm, "end": v(46.16, -30.16) * mm});
            skLineSegment(sketch, "E1081", {"start": v(46.16, -30.16) * mm, "end": v(45.9, -29.6) * mm});
            skLineSegment(sketch, "E1082", {"start": v(45.9, -29.6) * mm, "end": v(45.62, -29.09) * mm});
            skLineSegment(sketch, "E1083", {"start": v(45.62, -29.09) * mm, "end": v(45.35, -28.59) * mm});
            skLineSegment(sketch, "E1084", {"start": v(45.35, -28.59) * mm, "end": v(45.08, -28.12) * mm});
            skLineSegment(sketch, "E1085", {"start": v(45.08, -28.12) * mm, "end": v(44.8, -27.67) * mm});
            skLineSegment(sketch, "E1086", {"start": v(44.8, -27.67) * mm, "end": v(44.54, -27.25) * mm});
            skLineSegment(sketch, "E1087", {"start": v(44.54, -27.25) * mm, "end": v(44.27, -26.85) * mm});
            skLineSegment(sketch, "E1088", {"start": v(44.27, -26.85) * mm, "end": v(44.01, -26.48) * mm});
            skLineSegment(sketch, "E1089", {"start": v(44.01, -26.48) * mm, "end": v(43.75, -26.13) * mm});
            skLineSegment(sketch, "E1090", {"start": v(43.75, -26.13) * mm, "end": v(43.5, -25.8) * mm});
            skLineSegment(sketch, "E1091", {"start": v(43.5, -25.8) * mm, "end": v(43.26, -25.5) * mm});
            skLineSegment(sketch, "E1092", {"start": v(43.26, -25.5) * mm, "end": v(43.03, -25.22) * mm});
            skLineSegment(sketch, "E1093", {"start": v(43.03, -25.22) * mm, "end": v(42.8, -24.96) * mm});
            skLineSegment(sketch, "E1094", {"start": v(42.8, -24.96) * mm, "end": v(42.58, -24.72) * mm});
            skLineSegment(sketch, "E1095", {"start": v(42.58, -24.72) * mm, "end": v(42.38, -24.5) * mm});
            skLineSegment(sketch, "E1096", {"start": v(42.38, -24.5) * mm, "end": v(42.18, -24.31) * mm});
            skLineSegment(sketch, "E1097", {"start": v(42.18, -24.31) * mm, "end": v(42, -24.14) * mm});
            skLineSegment(sketch, "E1098", {"start": v(42, -24.14) * mm, "end": v(41.83, -23.98) * mm});
            skLineSegment(sketch, "E1099", {"start": v(41.83, -23.98) * mm, "end": v(41.67, -23.84) * mm});
            skLineSegment(sketch, "E1100", {"start": v(41.67, -23.84) * mm, "end": v(41.53, -23.72) * mm});
            skLineSegment(sketch, "E1101", {"start": v(41.53, -23.72) * mm, "end": v(41.4, -23.62) * mm});
            skLineSegment(sketch, "E1102", {"start": v(41.4, -23.62) * mm, "end": v(41.29, -23.53) * mm});
            skLineSegment(sketch, "E1103", {"start": v(41.29, -23.53) * mm, "end": v(41.2, -23.46) * mm});
            skLineSegment(sketch, "E1104", {"start": v(41.2, -23.46) * mm, "end": v(41.12, -23.4) * mm});
            skLineSegment(sketch, "E1105", {"start": v(41.12, -23.4) * mm, "end": v(41.05, -23.37) * mm});
            skLineSegment(sketch, "E1106", {"start": v(41.05, -23.37) * mm, "end": v(41, -23.34) * mm});
            skLineSegment(sketch, "E1107", {"start": v(41, -23.34) * mm, "end": v(40.98, -23.32) * mm});
            skLineSegment(sketch, "E1108", {"start": v(40.98, -23.32) * mm, "end": v(39.38, -22.4) * mm});
            skLineSegment(sketch, "E1109", {"start": v(39.38, -22.4) * mm, "end": v(41.86, -17.34) * mm});
            skLineSegment(sketch, "E1110", {"start": v(41.86, -17.34) * mm, "end": v(43.57, -18.05) * mm});
            skLineSegment(sketch, "E1111", {"start": v(43.57, -18.05) * mm, "end": v(43.6, -18.06) * mm});
            skLineSegment(sketch, "E1112", {"start": v(43.6, -18.06) * mm, "end": v(43.64, -18.07) * mm});
            skLineSegment(sketch, "E1113", {"start": v(43.64, -18.07) * mm, "end": v(43.71, -18.1) * mm});
            skLineSegment(sketch, "E1114", {"start": v(43.71, -18.1) * mm, "end": v(43.8, -18.13) * mm});
            skLineSegment(sketch, "E1115", {"start": v(43.8, -18.13) * mm, "end": v(43.92, -18.16) * mm});
            skLineSegment(sketch, "E1116", {"start": v(43.92, -18.16) * mm, "end": v(44.06, -18.2) * mm});
            skLineSegment(sketch, "E1117", {"start": v(44.06, -18.2) * mm, "end": v(44.22, -18.23) * mm});
            skLineSegment(sketch, "E1118", {"start": v(44.22, -18.23) * mm, "end": v(44.4, -18.27) * mm});
            skLineSegment(sketch, "E1119", {"start": v(44.4, -18.27) * mm, "end": v(44.6, -18.3) * mm});
            skLineSegment(sketch, "E1120", {"start": v(44.6, -18.3) * mm, "end": v(44.83, -18.35) * mm});
            skLineSegment(sketch, "E1121", {"start": v(44.83, -18.35) * mm, "end": v(45.08, -18.39) * mm});
            skLineSegment(sketch, "E1122", {"start": v(45.08, -18.39) * mm, "end": v(45.36, -18.42) * mm});
            skLineSegment(sketch, "E1123", {"start": v(45.36, -18.42) * mm, "end": v(45.65, -18.45) * mm});
            skLineSegment(sketch, "E1124", {"start": v(45.65, -18.45) * mm, "end": v(45.97, -18.48) * mm});
            skLineSegment(sketch, "E1125", {"start": v(45.97, -18.48) * mm, "end": v(46.31, -18.5) * mm});
            skLineSegment(sketch, "E1126", {"start": v(46.31, -18.5) * mm, "end": v(46.68, -18.5) * mm});
            skLineSegment(sketch, "E1127", {"start": v(46.68, -18.5) * mm, "end": v(47.07, -18.52) * mm});
            skLineSegment(sketch, "E1128", {"start": v(47.07, -18.52) * mm, "end": v(47.48, -18.51) * mm});
            skLineSegment(sketch, "E1129", {"start": v(47.48, -18.51) * mm, "end": v(47.91, -18.5) * mm});
            skLineSegment(sketch, "E1130", {"start": v(47.91, -18.5) * mm, "end": v(48.37, -18.48) * mm});
            skLineSegment(sketch, "E1131", {"start": v(48.37, -18.48) * mm, "end": v(48.84, -18.44) * mm});
            skLineSegment(sketch, "E1132", {"start": v(48.84, -18.44) * mm, "end": v(49.34, -18.4) * mm});
            skLineSegment(sketch, "E1133", {"start": v(49.34, -18.4) * mm, "end": v(49.86, -18.34) * mm});
            skLineSegment(sketch, "E1134", {"start": v(49.86, -18.34) * mm, "end": v(50.4, -18.26) * mm});
            skLineSegment(sketch, "E1135", {"start": v(50.4, -18.26) * mm, "end": v(50.96, -18.17) * mm});
            skLineSegment(sketch, "E1136", {"start": v(50.96, -18.17) * mm, "end": v(51.54, -18.06) * mm});
            skLineSegment(sketch, "E1137", {"start": v(51.54, -18.06) * mm, "end": v(52.14, -17.94) * mm});
            skLineSegment(sketch, "E1138", {"start": v(52.14, -17.94) * mm, "end": v(52.76, -17.8) * mm});
            skLineSegment(sketch, "E1139", {"start": v(52.76, -17.8) * mm, "end": v(53.4, -17.64) * mm});
            skLineSegment(sketch, "E1140", {"start": v(53.4, -17.64) * mm, "end": v(54.06, -17.46) * mm});
            skLineSegment(sketch, "E1141", {"start": v(54.06, -17.46) * mm, "end": v(54.73, -17.26) * mm});
            skLineSegment(sketch, "E1142", {"start": v(54.73, -17.26) * mm, "end": v(55.42, -17.04) * mm});
            skLineSegment(sketch, "E1143", {"start": v(55.42, -17.04) * mm, "end": v(56.12, -16.8) * mm});
            skLineSegment(sketch, "E1144", {"start": v(56.12, -16.8) * mm, "end": v(56.85, -16.52) * mm});
            skLineSegment(sketch, "E1145", {"start": v(56.85, -16.52) * mm, "end": v(57.3, -16.15) * mm});
            skLineSegment(sketch, "E1146", {"start": v(57.3, -16.15) * mm, "end": v(57.79, -14.3) * mm});
            skLineSegment(sketch, "E1147", {"start": v(57.79, -14.3) * mm, "end": v(57.58, -13.76) * mm});
            skLineSegment(sketch, "E1148", {"start": v(57.58, -13.76) * mm, "end": v(57.08, -13.17) * mm});
            skLineSegment(sketch, "E1149", {"start": v(57.08, -13.17) * mm, "end": v(56.6, -12.6) * mm});
            skLineSegment(sketch, "E1150", {"start": v(56.6, -12.6) * mm, "end": v(56.1, -12.07) * mm});
            skLineSegment(sketch, "E1151", {"start": v(56.1, -12.07) * mm, "end": v(55.62, -11.56) * mm});
            skLineSegment(sketch, "E1152", {"start": v(55.62, -11.56) * mm, "end": v(55.14, -11.08) * mm});
            skLineSegment(sketch, "E1153", {"start": v(55.14, -11.08) * mm, "end": v(54.66, -10.63) * mm});
            skLineSegment(sketch, "E1154", {"start": v(54.66, -10.63) * mm, "end": v(54.2, -10.2) * mm});
            skLineSegment(sketch, "E1155", {"start": v(54.2, -10.2) * mm, "end": v(53.73, -9.8) * mm});
            skLineSegment(sketch, "E1156", {"start": v(53.73, -9.8) * mm, "end": v(53.28, -9.41) * mm});
            skLineSegment(sketch, "E1157", {"start": v(53.28, -9.41) * mm, "end": v(52.84, -9.06) * mm});
            skLineSegment(sketch, "E1158", {"start": v(52.84, -9.06) * mm, "end": v(52.4, -8.73) * mm});
            skLineSegment(sketch, "E1159", {"start": v(52.4, -8.73) * mm, "end": v(51.98, -8.42) * mm});
            skLineSegment(sketch, "E1160", {"start": v(51.98, -8.42) * mm, "end": v(51.57, -8.13) * mm});
            skLineSegment(sketch, "E1161", {"start": v(51.57, -8.13) * mm, "end": v(51.18, -7.86) * mm});
            skLineSegment(sketch, "E1162", {"start": v(51.18, -7.86) * mm, "end": v(50.8, -7.62) * mm});
            skLineSegment(sketch, "E1163", {"start": v(50.8, -7.62) * mm, "end": v(50.42, -7.4) * mm});
            skLineSegment(sketch, "E1164", {"start": v(50.42, -7.4) * mm, "end": v(50.07, -7.19) * mm});
            skLineSegment(sketch, "E1165", {"start": v(50.07, -7.19) * mm, "end": v(49.73, -7) * mm});
            skLineSegment(sketch, "E1166", {"start": v(49.73, -7) * mm, "end": v(49.4, -6.83) * mm});
            skLineSegment(sketch, "E1167", {"start": v(49.4, -6.83) * mm, "end": v(49.1, -6.68) * mm});
            skLineSegment(sketch, "E1168", {"start": v(49.1, -6.68) * mm, "end": v(48.8, -6.54) * mm});
            skLineSegment(sketch, "E1169", {"start": v(48.8, -6.54) * mm, "end": v(48.53, -6.42) * mm});
            skLineSegment(sketch, "E1170", {"start": v(48.53, -6.42) * mm, "end": v(48.27, -6.32) * mm});
            skLineSegment(sketch, "E1171", {"start": v(48.27, -6.32) * mm, "end": v(48.04, -6.23) * mm});
            skLineSegment(sketch, "E1172", {"start": v(48.04, -6.23) * mm, "end": v(47.82, -6.15) * mm});
            skLineSegment(sketch, "E1173", {"start": v(47.82, -6.15) * mm, "end": v(47.62, -6.08) * mm});
            skLineSegment(sketch, "E1174", {"start": v(47.62, -6.08) * mm, "end": v(47.45, -6.02) * mm});
            skLineSegment(sketch, "E1175", {"start": v(47.45, -6.02) * mm, "end": v(47.29, -5.98) * mm});
            skLineSegment(sketch, "E1176", {"start": v(47.29, -5.98) * mm, "end": v(47.15, -5.94) * mm});
            skLineSegment(sketch, "E1177", {"start": v(47.15, -5.94) * mm, "end": v(47.04, -5.91) * mm});
            skLineSegment(sketch, "E1178", {"start": v(47.04, -5.91) * mm, "end": v(46.94, -5.9) * mm});
            skLineSegment(sketch, "E1179", {"start": v(46.94, -5.9) * mm, "end": v(46.87, -5.88) * mm});
            skLineSegment(sketch, "E1180", {"start": v(46.87, -5.88) * mm, "end": v(46.82, -5.87) * mm});
            skLineSegment(sketch, "E1181", {"start": v(46.82, -5.87) * mm, "end": v(46.79, -5.86) * mm});
            skLineSegment(sketch, "E1182", {"start": v(46.79, -5.86) * mm, "end": v(44.96, -5.63) * mm});
            skLineSegment(sketch, "E1183", {"start": v(44.96, -5.63) * mm, "end": v(45.31, 0) * mm});
            skLineSegment(sketch, "E1184", {"start": v(2.65, 0) * mm, "end": v(-2.65, 0) * mm});
            skLineSegment(sketch, "E1185", {"start": v(0, -2.65) * mm, "end": v(0, 2.65) * mm});
            skCircle(sketch, "E1186", {"center": v(0, 0) * mm, "radius": 3.52 * mm});
            skSolve(sketch);
        }
        {
            var Q0;
            Q0=makeQuery(id+"F0.imprint","IMPRINT",FACE,{"disambiguationData":[TD([[makeQuery(id+"F0.imprint","IMPRINT",EDGE,{"derivedFrom":sQuery(id+"F0.wireOp",EDGE,"E0")}),1.0]])]});
            extrude(context, id + "F1", {"entities" : qUnion([Q0]), "depth" : 6.5 * mm, "offsetDistance" : 25 * mm});
        }
    });
